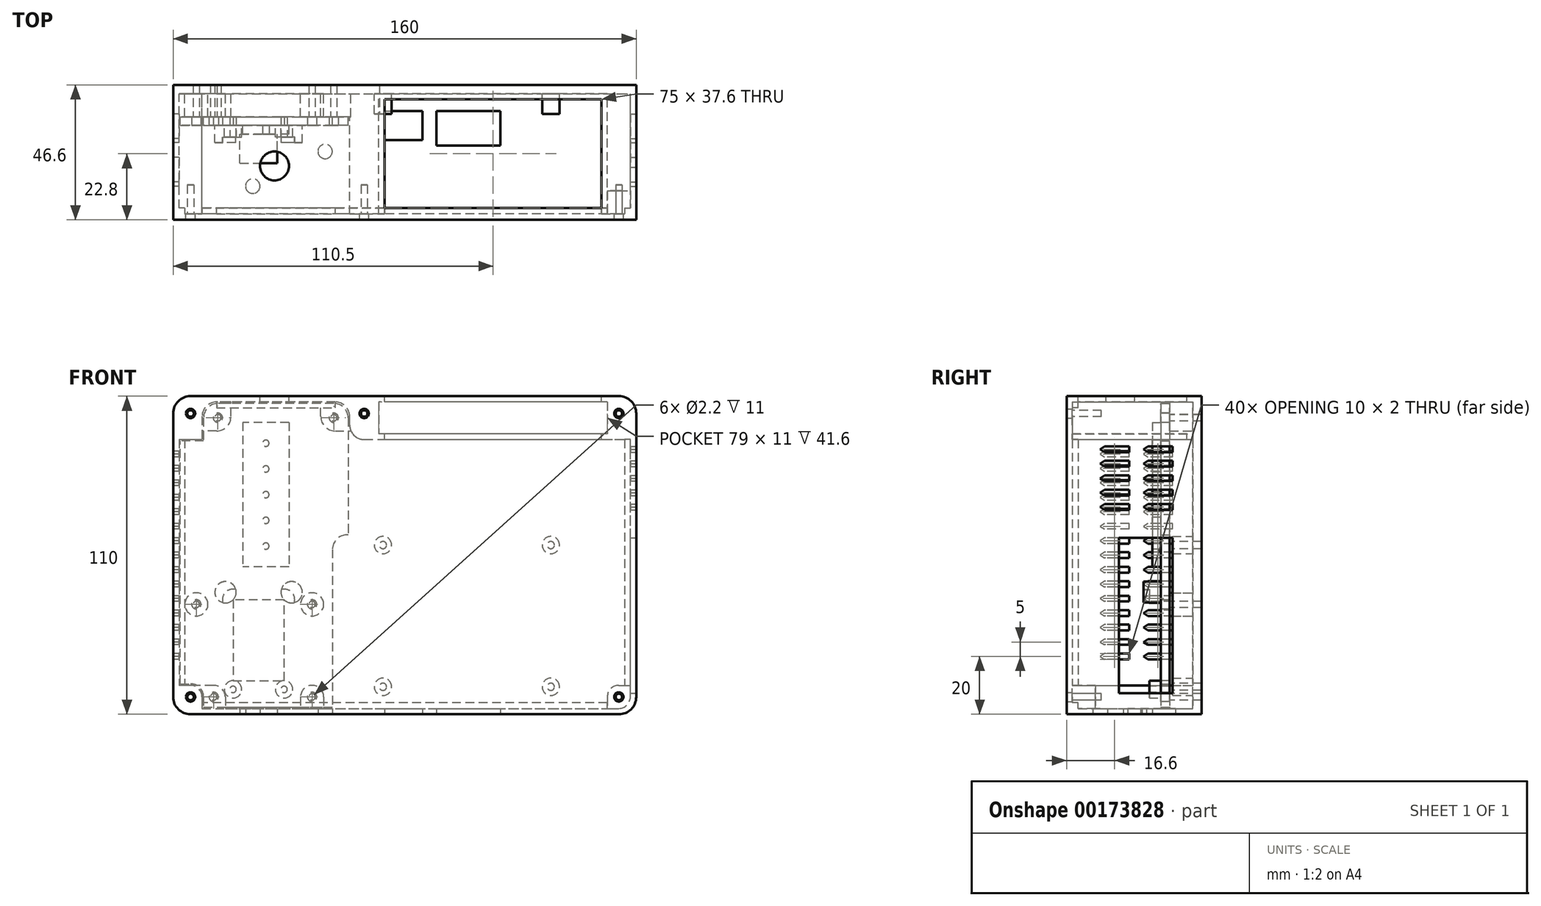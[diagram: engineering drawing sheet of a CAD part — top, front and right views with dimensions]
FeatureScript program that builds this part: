
annotation { "Feature Type Name" : "Feature", "Feature Type Description" : "" }
export const myFeature = defineFeature(function(context is Context, id is Id, definition is map)
    precondition{}
    {
        {
            var Q0;
            Q0=qCreatedBy(makeId("Front.planeOp"),FACE);
            var sketch = newSketch(context, id + "F0", { "sketchPlane" : qUnion([Q0])});
            skLineSegment(sketch, "E0.bottom", {"start": v(6, 0) * mm, "end": v(154, 0) * mm});
            skLineSegment(sketch, "E0.top", {"start": v(6, 110) * mm, "end": v(154, 110) * mm});
            skLineSegment(sketch, "E0.left", {"start": v(0, 6) * mm, "end": v(0, 104) * mm});
            skLineSegment(sketch, "E0.right", {"start": v(160, 6) * mm, "end": v(160, 104) * mm});
            skPoint(sketch, "E1.visualSharp", {"position": v(0, 110) * mm});
            skArc(sketch, "E1.filletArc", {"start": v(6, 110) * mm, "mid": v(1.76, 108.24) * mm, "end": v(0, 104) * mm});
            skPoint(sketch, "E2.visualSharp", {"position": v(160, 110) * mm});
            skArc(sketch, "E2.filletArc", {"start": v(160, 104) * mm, "mid": v(158.24, 108.24) * mm, "end": v(154, 110) * mm});
            skPoint(sketch, "E3.visualSharp", {"position": v(160, 0) * mm});
            skArc(sketch, "E3.filletArc", {"start": v(154, 0) * mm, "mid": v(158.24, 1.76) * mm, "end": v(160, 6) * mm});
            skPoint(sketch, "E4.visualSharp", {"position": v(0, 0) * mm});
            skArc(sketch, "E4.filletArc", {"start": v(0, 6) * mm, "mid": v(1.76, 1.76) * mm, "end": v(6, 0) * mm});
            skSolve(sketch);
        }
        {
            var Q0;
            Q0=makeQuery(id+"F0.imprint","IMPRINT",FACE,{"disambiguationData":[TD([[makeQuery(id+"F0.imprint","IMPRINT",EDGE,{"derivedFrom":sQuery(id+"F0.wireOp",EDGE,"E0.bottom")}),1.0]])]});
            extrude(context, id + "F1", {"entities" : qUnion([Q0]), "depth" : 3 * mm, "offsetDistance" : 25 * mm});
        }
        {
            var Q0;
            Q0=makeQuery(id+"F1.opExtrude","CAP_FACE",FACE,{"disambiguationData":[OSD([sQuery(id+"F0.wireOp",EDGE,"E0.bottom"),sQuery(id+"F0.wireOp",EDGE,"E0.top"),sQuery(id+"F0.wireOp",EDGE,"E0.left"),sQuery(id+"F0.wireOp",EDGE,"E0.right"),sQuery(id+"F0.wireOp",EDGE,"E1.filletArc"),sQuery(id+"F0.wireOp",EDGE,"E2.filletArc"),sQuery(id+"F0.wireOp",EDGE,"E3.filletArc"),sQuery(id+"F0.wireOp",EDGE,"E4.filletArc")])],"isStart":false});
            var sketch = newSketch(context, id + "F2", { "sketchPlane" : qUnion([Q0])});
            skLineSegment(sketch, "E5.bottom", {"start": v(150, 108) * mm, "end": v(150, 97) * mm});
            skLineSegment(sketch, "E5.top", {"start": v(71, 108) * mm, "end": v(71, 97) * mm});
            skLineSegment(sketch, "E5.left", {"start": v(150, 108) * mm, "end": v(80, 108) * mm});
            skLineSegment(sketch, "E5.right", {"start": v(150, 97) * mm, "end": v(71, 97) * mm});
            skLineSegment(sketch, "E6", {"start": v(71, 97) * mm, "end": v(71, 68) * mm, "construction": true});
            skLineSegment(sketch, "E7", {"start": v(71, 68) * mm, "end": v(150, 68) * mm, "construction": true});
            skLineSegment(sketch, "E8", {"start": v(150, 68) * mm, "end": v(150, 97) * mm, "construction": true});
            skLineSegment(sketch, "E9", {"start": v(71, 73) * mm, "end": v(150, 73) * mm, "construction": true});
            skLineSegment(sketch, "E10", {"start": v(80, 108) * mm, "end": v(71, 108) * mm});
            skPoint(sketch, "E11", {"position": v(80, 110) * mm});
            skLineSegment(sketch, "E12", {"start": v(2, 95) * mm, "end": v(10, 95) * mm});
            skLineSegment(sketch, "E13.0", {"start": v(6, 110) * mm, "end": v(154, 110) * mm});
            skPoint(sketch, "E14.0", {"position": v(1.76, 108.24) * mm});
            skLineSegment(sketch, "E15.0", {"start": v(0, 95) * mm, "end": v(0, 104) * mm});
            skArc(sketch, "E16.0", {"start": v(160, 104) * mm, "mid": v(158.24, 108.24) * mm, "end": v(154, 110) * mm});
            skLineSegment(sketch, "E17.0", {"start": v(160, 95) * mm, "end": v(160, 104) * mm});
            skPoint(sketch, "E18.orphan", {"position": v(0, 6) * mm});
            skPoint(sketch, "E19.orphan", {"position": v(160, 6) * mm});
            skPoint(sketch, "E20.orphan", {"position": v(10, 108) * mm});
            skLineSegment(sketch, "E21", {"start": v(61, 100) * mm, "end": v(61, 103) * mm});
            skLineSegment(sketch, "E22", {"start": v(56, 108) * mm, "end": v(15, 108) * mm});
            skLineSegment(sketch, "E23", {"start": v(10, 103) * mm, "end": v(10, 95) * mm});
            skArc(sketch, "E24.filletArc", {"start": v(15, 108) * mm, "mid": v(11.46, 106.54) * mm, "end": v(10, 103) * mm});
            skLineSegment(sketch, "E25.trimOffspring", {"start": v(66, 95) * mm, "end": v(158, 95) * mm});
            skPoint(sketch, "E26.0", {"position": v(1.76, 1.76) * mm});
            skLineSegment(sketch, "E27.0", {"start": v(6, 0) * mm, "end": v(84.03, 0) * mm});
            skPoint(sketch, "E28.orphan", {"position": v(154, 0) * mm});
            skArc(sketch, "E29.0", {"start": v(6, 110) * mm, "mid": v(1.76, 108.24) * mm, "end": v(0, 104) * mm});
            skLineSegment(sketch, "E30.0", {"start": v(160, 6) * mm, "end": v(160, 104) * mm});
            skLineSegment(sketch, "E31.0", {"start": v(0, 6) * mm, "end": v(0, 104) * mm});
            skArc(sketch, "E32.0", {"start": v(0, 6) * mm, "mid": v(1.76, 1.76) * mm, "end": v(6, 0) * mm});
            skLineSegment(sketch, "E33.0.2", {"start": v(154, 110) * mm, "end": v(6, 110) * mm});
            skLineSegment(sketch, "E33.0.4", {"start": v(0, 104) * mm, "end": v(0, 6) * mm});
            skLineSegment(sketch, "E33.0.6", {"start": v(6, 0) * mm, "end": v(154, 0) * mm});
            skArc(sketch, "E33.0.7", {"start": v(154, 0) * mm, "mid": v(158.24, 1.76) * mm, "end": v(160, 6) * mm});
            skLineSegment(sketch, "E34.0", {"start": v(158, 6) * mm, "end": v(158, 95) * mm});
            skLineSegment(sketch, "E34.1", {"start": v(2, 95) * mm, "end": v(2, 10) * mm});
            skLineSegment(sketch, "E34.3", {"start": v(10, 2) * mm, "end": v(154, 2) * mm});
            skArc(sketch, "E34.4", {"start": v(154, 2) * mm, "mid": v(156.83, 3.17) * mm, "end": v(158, 6) * mm});
            skPoint(sketch, "E35.visualSharp", {"position": v(61, 108) * mm});
            skArc(sketch, "E35.filletArc", {"start": v(61, 103) * mm, "mid": v(59.54, 106.54) * mm, "end": v(56, 108) * mm});
            skPoint(sketch, "E36.visualSharp", {"position": v(61, 95) * mm});
            skArc(sketch, "E36.filletArc", {"start": v(61, 100) * mm, "mid": v(62.46, 96.46) * mm, "end": v(66, 95) * mm});
            skArc(sketch, "E37", {"start": v(10, 6) * mm, "mid": v(8.83, 8.83) * mm, "end": v(6, 10) * mm});
            skLineSegment(sketch, "E38", {"start": v(10, 6) * mm, "end": v(10, 2) * mm});
            skLineSegment(sketch, "E39", {"start": v(6, 10) * mm, "end": v(2, 10) * mm});
            skSolve(sketch);
        }
        {
            var Q0;
            Q0=makeQuery(id+"F2.imprint","IMPRINT",FACE,{"disambiguationData":[TD([[makeQuery(id+"F2.imprint","IMPRINT",EDGE,{"derivedFrom":sQuery(id+"F2.wireOp",EDGE,"E5.bottom")}),1.0]])]});
            extrude(context, id + "F3", {"entities" : qUnion([Q0]), "operationType" : NewBodyOperationType.ADD, "depth" : 41.6 * mm, "offsetDistance" : 25 * mm});
        }
        {
            var Q0;
            Q0=qCreatedBy(makeId("Front.planeOp"),FACE);
            var sketch = newSketch(context, id + "F4", { "sketchPlane" : qUnion([Q0])});
            skLineSegment(sketch, "E40.bottom", {"start": v(69, 9.5) * mm, "end": v(69, 58.5) * mm, "construction": true});
            skLineSegment(sketch, "E40.top", {"start": v(154, 9.5) * mm, "end": v(154, 58.5) * mm, "construction": true});
            skLineSegment(sketch, "E40.left", {"start": v(72.5, 6) * mm, "end": v(150.5, 6) * mm, "construction": true});
            skLineSegment(sketch, "E40.right", {"start": v(72.5, 62) * mm, "end": v(150.5, 62) * mm, "construction": true});
            skPoint(sketch, "E41.visualSharp", {"position": v(69, 6) * mm});
            skArc(sketch, "E41.filletArc", {"start": v(69, 9.5) * mm, "mid": v(70.03, 7.03) * mm, "end": v(72.5, 6) * mm, "construction": true});
            skPoint(sketch, "E42.visualSharp", {"position": v(69, 62) * mm});
            skArc(sketch, "E42.filletArc", {"start": v(72.5, 62) * mm, "mid": v(70.03, 60.97) * mm, "end": v(69, 58.5) * mm, "construction": true});
            skPoint(sketch, "E43.visualSharp", {"position": v(154, 62) * mm});
            skArc(sketch, "E43.filletArc", {"start": v(154, 58.5) * mm, "mid": v(152.97, 60.97) * mm, "end": v(150.5, 62) * mm, "construction": true});
            skPoint(sketch, "E44.visualSharp", {"position": v(154, 6) * mm});
            skArc(sketch, "E44.filletArc", {"start": v(150.5, 6) * mm, "mid": v(152.97, 7.03) * mm, "end": v(154, 9.5) * mm, "construction": true});
            skCircle(sketch, "E45", {"center": v(72.5, 58.5) * mm, "radius": 3 * mm});
            skCircle(sketch, "E46", {"center": v(130.5, 58.5) * mm, "radius": 3 * mm});
            skCircle(sketch, "E47", {"center": v(130.5, 9.5) * mm, "radius": 3 * mm});
            skCircle(sketch, "E48", {"center": v(72.5, 9.5) * mm, "radius": 3 * mm});
            skPoint(sketch, "E49.0", {"position": v(6, 104) * mm});
            skPoint(sketch, "E50.0", {"position": v(154, 104) * mm});
            skPoint(sketch, "E51.0", {"position": v(6, 6) * mm});
            skPoint(sketch, "E52.orphan", {"position": v(6, 0) * mm});
            skPoint(sketch, "E53.0.end.orphan", {"position": v(160, 104) * mm});
            skPoint(sketch, "E53.0.start.orphan", {"position": v(160, 6) * mm});
            skSolve(sketch);
        }
        {
            var Q0;
            Q0=makeQuery(id+"F3.boolean.opBoolean","MERGE",FACE,{"derivedFrom":[makeQuery(id+"F1.opExtrude","SWEPT_FACE",FACE,{"disambiguationData":[OSD([sQuery(id+"F0.wireOp",EDGE,"E0.top")])]}),makeQuery(id+"F3.opExtrude","SWEPT_FACE",FACE,{"disambiguationData":[OSD([sQuery(id+"F2.wireOp",EDGE,"E13.0")])]})]});
            var sketch = newSketch(context, id + "F5", { "sketchPlane" : qUnion([Q0])});
            skLineSegment(sketch, "E54.bottom", {"start": v(73, -44.6) * mm, "end": v(148, -44.6) * mm});
            skLineSegment(sketch, "E54.top", {"start": v(73, -5) * mm, "end": v(148, -5) * mm});
            skLineSegment(sketch, "E54.left", {"start": v(73, -44.6) * mm, "end": v(73, -5) * mm});
            skLineSegment(sketch, "E54.right", {"start": v(148, -44.6) * mm, "end": v(148, -5) * mm});
            skLineSegment(sketch, "E55.0", {"start": v(71, -44.6) * mm, "end": v(71, -3) * mm});
            skLineSegment(sketch, "E56.0", {"start": v(150, -44.6) * mm, "end": v(150, -3) * mm});
            skLineSegment(sketch, "E57.0", {"start": v(150, -3) * mm, "end": v(71, -3) * mm});
            skSolve(sketch);
        }
        {
            var Q0;
            Q0 = qSketchRegion(id + "F5", true);
            extrude(context, id + "F6", {"entities" : qUnion([Q0]), "operationType" : NewBodyOperationType.REMOVE, "oppositeDirection" : true, "depth" : 19.9 * mm, "offsetDistance" : 25 * mm});
        }
        {
            var Q0;
            Q0 = qSketchRegion(id + "F4", true);
            var Q1;
            Q1=sQuery(id+"F4.wireOp",EDGE,"E46");
            var Q2;
            Q2=sQuery(id+"F4.wireOp",EDGE,"E45");
            var Q3;
            Q3=sQuery(id+"F4.wireOp",EDGE,"E48");
            var Q4;
            Q4=sQuery(id+"F4.wireOp",EDGE,"E47");
            extrude(context, id + "F7", {"entities" : qUnion([Q0]), "operationType" : NewBodyOperationType.ADD, "surfaceEntities" : qUnion([Q1, Q2, Q3, Q4]), "depth" : 10 * mm, "offsetDistance" : 25 * mm});
        }
        {
            var Q0;
            Q0=makeQuery(id+"F7.opExtrude","CAP_FACE",FACE,{"disambiguationData":[OSD([sQuery(id+"F4.wireOp",EDGE,"E45")])],"isStart":false});
            var sketch = newSketch(context, id + "F8", { "sketchPlane" : qUnion([Q0])});
            skPoint(sketch, "E58.0", {"position": v(72.5, 58.5) * mm});
            skPoint(sketch, "E59.0", {"position": v(130.5, 58.5) * mm});
            skPoint(sketch, "E60.0", {"position": v(130.5, 9.5) * mm});
            skPoint(sketch, "E61.0", {"position": v(72.5, 9.5) * mm});
            skCircle(sketch, "E62", {"center": v(72.5, 58.5) * mm, "radius": 1.25 * mm});
            skCircle(sketch, "E63", {"center": v(130.5, 58.5) * mm, "radius": 1.25 * mm});
            skCircle(sketch, "E64", {"center": v(130.5, 9.5) * mm, "radius": 1.25 * mm});
            skCircle(sketch, "E65", {"center": v(72.5, 9.5) * mm, "radius": 1.25 * mm});
            skSolve(sketch);
        }
        {
            var Q0;
            Q0 = qSketchRegion(id + "F8", true);
            extrude(context, id + "F9", {"entities" : qUnion([Q0]), "operationType" : NewBodyOperationType.REMOVE, "endBound" : BoundingType.UP_TO_NEXT, "oppositeDirection" : true, "depth" : 25 * mm, "offsetDistance" : 25 * mm});
        }
        {
            var Q0;
            Q0=qCreatedBy(makeId("Front.planeOp"),FACE);
            cPlane(context, id + "F10", {"entities" : qUnion([Q0]), "cplaneType" : CPlaneType.OFFSET, "offset" : 11 * mm, "width" : 150 * mm, "height" : 150 * mm});
        }
        {
            var Q0;
            Q0=qCreatedBy(id+"F10.planeOp",FACE);
            var sketch = newSketch(context, id + "F11", { "sketchPlane" : qUnion([Q0])});
            skPoint(sketch, "E66.0", {"position": v(10, 99) * mm});
            skPoint(sketch, "E67.0.start.orphan", {"position": v(61, 100) * mm});
            skLineSegment(sketch, "E68", {"start": v(60.5, 102.5) * mm, "end": v(60.5, 62) * mm});
            skPoint(sketch, "E69.0.start.orphan", {"position": v(15, 108) * mm});
            skPoint(sketch, "E70.0.start.orphan", {"position": v(10, 103) * mm});
            skPoint(sketch, "E71.end.orphan", {"position": v(10, 95) * mm});
            skPoint(sketch, "E72.0", {"position": v(35.5, 108) * mm});
            skPoint(sketch, "E73.0", {"position": v(6, 95) * mm});
            skLineSegment(sketch, "E74", {"start": v(55.5, 107.5) * mm, "end": v(15.45, 107.5) * mm});
            skLineSegment(sketch, "E75", {"start": v(10.5, 102.55) * mm, "end": v(10.5, 94.5) * mm});
            skLineSegment(sketch, "E76", {"start": v(10.5, 94.5) * mm, "end": v(2.5, 94.5) * mm});
            skPoint(sketch, "E77.visualSharp", {"position": v(10.5, 107.5) * mm});
            skArc(sketch, "E77.filletArc", {"start": v(15.45, 107.5) * mm, "mid": v(11.95, 106.05) * mm, "end": v(10.5, 102.55) * mm});
            skPoint(sketch, "E78.orphan", {"position": v(0, 104) * mm});
            skPoint(sketch, "E79.orphan", {"position": v(154, 0) * mm});
            skLineSegment(sketch, "E80.0", {"start": v(2.5, 10.5) * mm, "end": v(2.5, 94.5) * mm});
            skLineSegment(sketch, "E80.2", {"start": v(10.5, 2.5) * mm, "end": v(55, 2.5) * mm});
            skPoint(sketch, "E81.0.end.orphan", {"position": v(6, 0) * mm});
            skPoint(sketch, "E82.0.start.orphan", {"position": v(0, 6) * mm});
            skPoint(sketch, "E83.orphan", {"position": v(0, 94.5) * mm});
            skPoint(sketch, "E84.visualSharp", {"position": v(60.5, 107.5) * mm});
            skArc(sketch, "E84.filletArc", {"start": v(60.5, 102.5) * mm, "mid": v(59.04, 106.04) * mm, "end": v(55.5, 107.5) * mm});
            skPoint(sketch, "E85.0.start.orphan", {"position": v(56, 108) * mm});
            skLineSegment(sketch, "E86", {"start": v(55, 32.32) * mm, "end": v(55, 2.5) * mm});
            skPoint(sketch, "E87.0", {"position": v(69, 62) * mm});
            skLineSegment(sketch, "E88", {"start": v(60.5, 62) * mm, "end": v(60, 62) * mm});
            skLineSegment(sketch, "E89", {"start": v(55, 57) * mm, "end": v(55, 32.32) * mm});
            skPoint(sketch, "E90.visualSharp", {"position": v(55, 62) * mm});
            skArc(sketch, "E90.filletArc", {"start": v(60, 62) * mm, "mid": v(56.46, 60.54) * mm, "end": v(55, 57) * mm});
            skLineSegment(sketch, "E91", {"start": v(2.5, 10.5) * mm, "end": v(6, 10.5) * mm});
            skLineSegment(sketch, "E92", {"start": v(10.5, 6) * mm, "end": v(10.5, 2.5) * mm});
            skPoint(sketch, "E93.0", {"position": v(6, 6) * mm});
            skArc(sketch, "E94", {"start": v(10.5, 6) * mm, "mid": v(9.18, 9.18) * mm, "end": v(6, 10.5) * mm});
            skSolve(sketch);
        }
        {
            var Q0;
            Q0 = qSketchRegion(id + "F11", true);
            extrude(context, id + "F12", {"entities" : qUnion([Q0]), "depth" : 3 * mm, "offsetDistance" : 25 * mm});
        }
        {
            var Q0;
            Q0=makeQuery(id+"F3.boolean.opBoolean","MERGE",FACE,{"derivedFrom":[makeQuery(id+"F1.opExtrude","SWEPT_FACE",FACE,{"disambiguationData":[OSD([sQuery(id+"F0.wireOp",EDGE,"E0.right")])]}),makeQuery(id+"F3.opExtrude","SWEPT_FACE",FACE,{"disambiguationData":[OSD([sQuery(id+"F2.wireOp",EDGE,"E30.0")])]})]});
            var sketch = newSketch(context, id + "F13", { "sketchPlane" : qUnion([Q0])});
            skLineSegment(sketch, "E95.left", {"start": v(-28.5, 7.25) * mm, "end": v(-28.5, 44.5) * mm});
            skLineSegment(sketch, "E95.right", {"start": v(-10, 7.25) * mm, "end": v(-10, 16.25) * mm});
            skPoint(sketch, "E96.0", {"position": v(0, 6) * mm});
            skLineSegment(sketch, "E97", {"start": v(-10, 16.25) * mm, "end": v(-10, 45) * mm});
            skLineSegment(sketch, "E98.top", {"start": v(-10, 61) * mm, "end": v(-28.5, 61) * mm});
            skLineSegment(sketch, "E98.left", {"start": v(-10, 45) * mm, "end": v(-10, 53) * mm});
            skLineSegment(sketch, "E98.right", {"start": v(-28.5, 44.5) * mm, "end": v(-28.5, 61) * mm});
            skLineSegment(sketch, "E99", {"start": v(-10, 53) * mm, "end": v(-10, 61) * mm});
            skLineSegment(sketch, "E100", {"start": v(-10, 7.25) * mm, "end": v(-28.5, 7.25) * mm});
            skSolve(sketch);
        }
        {
            var Q0;
            Q0 = qSketchRegion(id + "F13", true);
            extrude(context, id + "F14", {"entities" : qUnion([Q0]), "operationType" : NewBodyOperationType.REMOVE, "endBound" : BoundingType.UP_TO_NEXT, "oppositeDirection" : true, "depth" : 25 * mm, "offsetDistance" : 25 * mm});
        }
        {
            var Q0;
            Q0=makeQuery(id+"F3.boolean.opBoolean","MERGE",FACE,{"derivedFrom":[makeQuery(id+"F1.opExtrude","SWEPT_FACE",FACE,{"disambiguationData":[OSD([sQuery(id+"F0.wireOp",EDGE,"E0.bottom")])]}),makeQuery(id+"F3.opExtrude","SWEPT_FACE",FACE,{"disambiguationData":[OSD([sQuery(id+"F2.wireOp",EDGE,"E33.0.6")])]})]});
            var sketch = newSketch(context, id + "F15", { "sketchPlane" : qUnion([Q0])});
            skLineSegment(sketch, "E101.bottom", {"start": v(73.1, 19) * mm, "end": v(73.1, 9) * mm});
            skLineSegment(sketch, "E101.top", {"start": v(86.1, 19) * mm, "end": v(86.1, 9) * mm});
            skLineSegment(sketch, "E101.left", {"start": v(73.1, 19) * mm, "end": v(86.1, 19) * mm});
            skLineSegment(sketch, "E101.right", {"start": v(73.1, 9) * mm, "end": v(79.6, 9) * mm});
            skPoint(sketch, "E102.0", {"position": v(72.93, 1.92) * mm});
            skLineSegment(sketch, "E103", {"start": v(79.6, 9) * mm, "end": v(86.1, 9) * mm});
            skLineSegment(sketch, "E104.bottom", {"start": v(91, 9) * mm, "end": v(91, 21) * mm});
            skLineSegment(sketch, "E104.top", {"start": v(113, 9) * mm, "end": v(113, 21) * mm});
            skLineSegment(sketch, "E104.left", {"start": v(91, 9) * mm, "end": v(102, 9) * mm});
            skLineSegment(sketch, "E104.right", {"start": v(91, 21) * mm, "end": v(113, 21) * mm});
            skLineSegment(sketch, "E105", {"start": v(102, 9) * mm, "end": v(113, 9) * mm});
            skLineSegment(sketch, "E106.bottom", {"start": v(23, 27) * mm, "end": v(23, 17) * mm});
            skLineSegment(sketch, "E106.top", {"start": v(36, 27) * mm, "end": v(36, 17) * mm});
            skLineSegment(sketch, "E106.left", {"start": v(23, 27) * mm, "end": v(36, 27) * mm});
            skLineSegment(sketch, "E106.right", {"start": v(23, 17) * mm, "end": v(29.5, 17) * mm});
            skLineSegment(sketch, "E107", {"start": v(29.5, 17) * mm, "end": v(36, 17) * mm});
            skSolve(sketch);
        }
        {
            var Q0;
            Q0=makeQuery(id+"F3.boolean.opBoolean","MERGE",FACE,{"derivedFrom":[makeQuery(id+"F1.opExtrude","SWEPT_FACE",FACE,{"disambiguationData":[OSD([sQuery(id+"F0.wireOp",EDGE,"E0.bottom")])]}),makeQuery(id+"F3.opExtrude","SWEPT_FACE",FACE,{"disambiguationData":[OSD([sQuery(id+"F2.wireOp",EDGE,"E33.0.6")])]})]});
            var sketch = newSketch(context, id + "F16", { "sketchPlane" : qUnion([Q0])});
            skCircle(sketch, "E108", {"center": v(27.5, 35) * mm, "radius": 2.5 * mm});
            skCircle(sketch, "E109", {"center": v(52.5, 23) * mm, "radius": 2.5 * mm});
            skPoint(sketch, "E110", {"position": v(34, 23) * mm});
            skPoint(sketch, "E111", {"position": v(27.5, 26) * mm});
            skSolve(sketch);
        }
        {
            var Q0;
            Q0=makeQuery(id+"F15.imprint","IMPRINT",FACE,{"disambiguationData":[TD([[makeQuery(id+"F15.imprint","IMPRINT",EDGE,{"derivedFrom":sQuery(id+"F15.wireOp",EDGE,"E106.bottom")}),1.0]])]});
            var Q1;
            Q1=makeQuery(id+"F15.imprint","IMPRINT",FACE,{"disambiguationData":[TD([[makeQuery(id+"F15.imprint","IMPRINT",EDGE,{"derivedFrom":sQuery(id+"F15.wireOp",EDGE,"E101.bottom")}),1.0]])]});
            var Q2;
            Q2=makeQuery(id+"F15.imprint","IMPRINT",FACE,{"disambiguationData":[TD([[makeQuery(id+"F15.imprint","IMPRINT",EDGE,{"derivedFrom":sQuery(id+"F15.wireOp",EDGE,"E104.bottom")}),-1.0]])]});
            var Q3;
            Q3 = qSketchRegion(id + "F16", true);
            extrude(context, id + "F17", {"entities" : qUnion([Q0, Q1, Q2, Q3]), "operationType" : NewBodyOperationType.REMOVE, "endBound" : BoundingType.UP_TO_NEXT, "oppositeDirection" : true, "depth" : 25 * mm, "offsetDistance" : 25 * mm});
        }
        {
            var Q0;
            Q0=makeQuery(id+"F12.opExtrude","CAP_FACE",FACE,{"disambiguationData":[OSD([sQuery(id+"F11.wireOp",EDGE,"E68"),sQuery(id+"F11.wireOp",EDGE,"E74"),sQuery(id+"F11.wireOp",EDGE,"E75"),sQuery(id+"F11.wireOp",EDGE,"E76"),sQuery(id+"F11.wireOp",EDGE,"E77.filletArc"),sQuery(id+"F11.wireOp",EDGE,"E80.0"),sQuery(id+"F11.wireOp",EDGE,"E80.1"),sQuery(id+"F11.wireOp",EDGE,"E80.2")])],"isStart":false});
            var sketch = newSketch(context, id + "F18", { "sketchPlane" : qUnion([Q0])});
            skLineSegment(sketch, "E112.bottom", {"start": v(20.68, 42.2) * mm, "end": v(38.32, 42.2) * mm, "construction": true});
            skLineSegment(sketch, "E112.top", {"start": v(20.67, 6) * mm, "end": v(29.5, 6) * mm, "construction": true});
            skLineSegment(sketch, "E112.left", {"start": v(18.07, 39.6) * mm, "end": v(18.07, 8.6) * mm, "construction": true});
            skLineSegment(sketch, "E112.right", {"start": v(40.93, 39.6) * mm, "end": v(40.93, 8.6) * mm, "construction": true});
            skPoint(sketch, "E113.visualSharp", {"position": v(18.07, 42.2) * mm});
            skArc(sketch, "E113.filletArc", {"start": v(20.67, 42.2) * mm, "mid": v(18.83, 41.44) * mm, "end": v(18.07, 39.6) * mm, "construction": true});
            skPoint(sketch, "E114.visualSharp", {"position": v(40.93, 42.2) * mm});
            skArc(sketch, "E114.filletArc", {"start": v(40.93, 39.6) * mm, "mid": v(40.17, 41.44) * mm, "end": v(38.32, 42.2) * mm});
            skPoint(sketch, "E115.visualSharp", {"position": v(40.93, 6) * mm});
            skArc(sketch, "E115.filletArc", {"start": v(38.33, 6) * mm, "mid": v(40.17, 6.76) * mm, "end": v(40.93, 8.6) * mm, "construction": true});
            skPoint(sketch, "E116.visualSharp", {"position": v(18.07, 6) * mm});
            skArc(sketch, "E116.filletArc", {"start": v(18.07, 8.6) * mm, "mid": v(18.83, 6.76) * mm, "end": v(20.67, 6) * mm, "construction": true});
            skCircle(sketch, "E117", {"center": v(20.68, 8.6) * mm, "radius": 1.1 * mm, "construction": true});
            skCircle(sketch, "E118", {"center": v(38.33, 8.6) * mm, "radius": 1.1 * mm, "construction": true});
            skCircle(sketch, "E119", {"center": v(20.68, 8.6) * mm, "radius": 3 * mm});
            skCircle(sketch, "E120", {"center": v(38.33, 8.6) * mm, "radius": 3 * mm});
            skCircle(sketch, "E121", {"center": v(40.93, 42.2) * mm, "radius": 3.68 * mm});
            skCircle(sketch, "E122", {"center": v(18.07, 42.2) * mm, "radius": 3.68 * mm});
            skLineSegment(sketch, "E123", {"start": v(29.5, 6) * mm, "end": v(38.33, 6) * mm, "construction": true});
            skSolve(sketch);
        }
        {
            var Q0;
            Q0 = qSketchRegion(id + "F18", true);
            extrude(context, id + "F19", {"entities" : qUnion([Q0]), "operationType" : NewBodyOperationType.ADD, "depth" : 4 * mm, "offsetDistance" : 25 * mm});
        }
        {
            var Q0;
            Q0=makeQuery(id+"F19.opExtrude","CAP_FACE",FACE,{"disambiguationData":[OSD([sQuery(id+"F18.wireOp",EDGE,"E119")])],"isStart":false});
            var sketch = newSketch(context, id + "F20", { "sketchPlane" : qUnion([Q0])});
            skPoint(sketch, "E124.0", {"position": v(20.68, 8.6) * mm});
            skPoint(sketch, "E125.0", {"position": v(38.33, 8.6) * mm});
            skCircle(sketch, "E126.0", {"center": v(20.68, 8.6) * mm, "radius": 1.1 * mm});
            skCircle(sketch, "E127.0", {"center": v(38.33, 8.6) * mm, "radius": 1.1 * mm});
            skSolve(sketch);
        }
        {
            var Q0;
            Q0 = qSketchRegion(id + "F20", true);
            extrude(context, id + "F21", {"entities" : qUnion([Q0]), "operationType" : NewBodyOperationType.REMOVE, "endBound" : BoundingType.UP_TO_NEXT, "oppositeDirection" : true, "depth" : 25 * mm, "offsetDistance" : 25 * mm});
        }
        {
            var Q0;
            Q0=makeQuery(id+"F18.imprint","IMPRINT",FACE,{"disambiguationData":[TD([[makeQuery(id+"F18.imprint","IMPRINT",EDGE,{"derivedFrom":sQuery(id+"F18.wireOp",EDGE,"E119")}),-1.0]])]});
            var sketch = newSketch(context, id + "F22", { "sketchPlane" : qUnion([Q0])});
            skLineSegment(sketch, "E128", {"start": v(20.68, 11.6) * mm, "end": v(20.68, 39.6) * mm});
            skLineSegment(sketch, "E129", {"start": v(20.68, 39.6) * mm, "end": v(38.32, 39.6) * mm});
            skLineSegment(sketch, "E130", {"start": v(38.32, 39.6) * mm, "end": v(38.32, 11.6) * mm});
            skLineSegment(sketch, "E131", {"start": v(38.32, 11.6) * mm, "end": v(20.68, 11.6) * mm});
            skPoint(sketch, "E132.0", {"position": v(20.68, 39.6) * mm});
            skPoint(sketch, "E133.0", {"position": v(38.32, 39.6) * mm});
            skSolve(sketch);
        }
        {
            var Q0;
            Q0 = qSketchRegion(id + "F22", true);
            extrude(context, id + "F23", {"entities" : qUnion([Q0]), "operationType" : NewBodyOperationType.REMOVE, "endBound" : BoundingType.UP_TO_NEXT, "oppositeDirection" : true, "depth" : 25 * mm, "offsetDistance" : 25 * mm});
        }
        {
            var Q0;
            Q0=makeQuery(id+"F19.opExtrude","CAP_FACE",FACE,{"disambiguationData":[OSD([sQuery(id+"F18.wireOp",EDGE,"E121")])],"isStart":false});
            var sketch = newSketch(context, id + "F24", { "sketchPlane" : qUnion([Q0])});
            skPoint(sketch, "E134.0", {"position": v(20.68, 39.6) * mm});
            skPoint(sketch, "E135.0", {"position": v(38.32, 39.6) * mm});
            skArc(sketch, "E136.0", {"start": v(21.63, 43.15) * mm, "mid": v(15.46, 44.8) * mm, "end": v(17.12, 38.64) * mm});
            skArc(sketch, "E137", {"start": v(21.63, 43.15) * mm, "mid": v(18.07, 42.2) * mm, "end": v(17.12, 38.64) * mm});
            skArc(sketch, "E138.converted", {"start": v(41.88, 38.64) * mm, "mid": v(43.53, 44.8) * mm, "end": v(37.37, 43.15) * mm});
            skArc(sketch, "E139.converted", {"start": v(41.88, 38.64) * mm, "mid": v(40.93, 42.2) * mm, "end": v(37.37, 43.15) * mm});
            skSolve(sketch);
        }
        {
            var Q0;
            Q0=makeQuery(id+"F24.imprint","IMPRINT",FACE,{"disambiguationData":[TD([[makeQuery(id+"F24.imprint","IMPRINT",EDGE,{"derivedFrom":sQuery(id+"F24.wireOp",EDGE,"E136.0")}),1.0]])]});
            var Q1;
            Q1=makeQuery(id+"F24.imprint","IMPRINT",FACE,{"disambiguationData":[TD([[makeQuery(id+"F24.imprint","IMPRINT",EDGE,{"derivedFrom":sQuery(id+"F24.wireOp",EDGE,"E138.converted")}),1.0]])]});
            extrude(context, id + "F25", {"entities" : qUnion([Q0, Q1]), "operationType" : NewBodyOperationType.ADD, "depth" : 2 * mm, "offsetDistance" : 25 * mm});
        }
        {
            var Q0;
            Q0=makeQuery(id+"F12.opExtrude","CAP_FACE",FACE,{"disambiguationData":[OSD([sQuery(id+"F11.wireOp",EDGE,"E68"),sQuery(id+"F11.wireOp",EDGE,"E74"),sQuery(id+"F11.wireOp",EDGE,"E75"),sQuery(id+"F11.wireOp",EDGE,"E76"),sQuery(id+"F11.wireOp",EDGE,"E77.filletArc"),sQuery(id+"F11.wireOp",EDGE,"E80.0"),sQuery(id+"F11.wireOp",EDGE,"E80.1"),sQuery(id+"F11.wireOp",EDGE,"E80.2")])],"isStart":false});
            var sketch = newSketch(context, id + "F26", { "sketchPlane" : qUnion([Q0])});
            skLineSegment(sketch, "E140.top", {"start": v(24.02, 100.94) * mm, "end": v(24.02, 50.94) * mm});
            skLineSegment(sketch, "E140.left", {"start": v(40.02, 100.94) * mm, "end": v(32.02, 100.94) * mm});
            skLineSegment(sketch, "E140.right", {"start": v(40.02, 50.94) * mm, "end": v(24.02, 50.94) * mm});
            skLineSegment(sketch, "E141", {"start": v(40.02, 100.94) * mm, "end": v(40.02, 75.94) * mm});
            skLineSegment(sketch, "E142", {"start": v(40.02, 75.94) * mm, "end": v(40.02, 50.94) * mm});
            skLineSegment(sketch, "E143", {"start": v(32.02, 100.94) * mm, "end": v(24.02, 100.94) * mm});
            skPoint(sketch, "E144", {"position": v(32.02, 58.16) * mm});
            skPoint(sketch, "E145.0.1.0", {"position": v(32.02, 67.05) * mm});
            skPoint(sketch, "E145.0.2.0", {"position": v(32.02, 75.94) * mm});
            skPoint(sketch, "E145.0.3.0", {"position": v(32.02, 84.83) * mm});
            skPoint(sketch, "E145.0.4.0", {"position": v(32.02, 93.72) * mm});
            skLineSegment(sketch, "E145.direction1", {"start": v(32.02, 58.16) * mm, "end": v(57.02, 58.16) * mm, "construction": true});
            skLineSegment(sketch, "E145.direction2", {"start": v(32.02, 58.16) * mm, "end": v(32.02, 67.05) * mm, "construction": true});
            skSolve(sketch);
        }
        {
            var Q0;
            Q0 = qSketchRegion(id + "F26", true);
            extrude(context, id + "F27", {"entities" : qUnion([Q0]), "operationType" : NewBodyOperationType.ADD, "depth" : 3 * mm, "offsetDistance" : 25 * mm});
        }
        {
            var Q0;
            Q0=sQuery(id+"F26.wireOp",VERTEX,"E145.0.4.0");
            var Q1;
            Q1=sQuery(id+"F26.wireOp",VERTEX,"E145.0.3.0");
            var Q2;
            Q2=sQuery(id+"F26.wireOp",VERTEX,"E145.0.2.0");
            var Q3;
            Q3=sQuery(id+"F26.wireOp",VERTEX,"E145.0.1.0");
            var Q4;
            Q4=sQuery(id+"F26.wireOp",VERTEX,"E144");
            var Q5;
            Q5=makeQuery(id+"F12.opExtrude","SWEPT_BODY",BODY,{"disambiguationData":[OSD([sQuery(id+"F11.wireOp",EDGE,"E68"),sQuery(id+"F11.wireOp",EDGE,"E74"),sQuery(id+"F11.wireOp",EDGE,"E75"),sQuery(id+"F11.wireOp",EDGE,"E76"),sQuery(id+"F11.wireOp",EDGE,"E77.filletArc"),sQuery(id+"F11.wireOp",EDGE,"E80.0"),sQuery(id+"F11.wireOp",EDGE,"E80.1"),sQuery(id+"F11.wireOp",EDGE,"E80.2"),sQuery(id+"F11.wireOp",EDGE,"E84.filletArc"),sQuery(id+"F11.wireOp",EDGE,"E86"),sQuery(id+"F11.wireOp",EDGE,"E88"),sQuery(id+"F11.wireOp",EDGE,"E89"),sQuery(id+"F11.wireOp",EDGE,"E90.filletArc")])]});
            hole(context, id + "F28", {"style" : HoleStyle.SIMPLE, "endStyle" : HoleEndStyle.THROUGH, "oppositeDirection" : true, "holeDiameter" : 2.2 * mm, "majorDiameter" : 5 * mm, "isTappedThrough" : true, "tappedDepth" : 12 * mm, "tapClearance" : 3, "locations" : qUnion([Q0, Q1, Q2, Q3, Q4]), "scope" : qUnion([Q5])});
        }
        {
            var Q0;
            Q0=makeQuery(id+"F3.boolean.opBoolean","SPLIT",FACE,{"disambiguationData":[TD([makeQuery(id+"F3.opExtrude","SWEPT_FACE",FACE,{"disambiguationData":[OSD([sQuery(id+"F2.wireOp",EDGE,"E12")])]})])],"derivedFrom":makeQuery(id+"F1.opExtrude","CAP_FACE",FACE,{"disambiguationData":[OSD([sQuery(id+"F0.wireOp",EDGE,"E0.bottom"),sQuery(id+"F0.wireOp",EDGE,"E0.top"),sQuery(id+"F0.wireOp",EDGE,"E0.left"),sQuery(id+"F0.wireOp",EDGE,"E0.right"),sQuery(id+"F0.wireOp",EDGE,"E1.filletArc"),sQuery(id+"F0.wireOp",EDGE,"E2.filletArc"),sQuery(id+"F0.wireOp",EDGE,"E3.filletArc"),sQuery(id+"F0.wireOp",EDGE,"E4.filletArc")])],"isStart":false})});
            var sketch = newSketch(context, id + "F29", { "sketchPlane" : qUnion([Q0])});
            skArc(sketch, "E146", {"start": v(15, 98) * mm, "mid": v(18.54, 99.46) * mm, "end": v(20, 103) * mm});
            skArc(sketch, "E147", {"start": v(51, 103) * mm, "mid": v(52.46, 99.46) * mm, "end": v(56, 98) * mm});
            skArc(sketch, "E148", {"start": v(44, 6) * mm, "mid": v(48, 10) * mm, "end": v(52, 6) * mm});
            skCircle(sketch, "E149", {"center": v(8, 38) * mm, "radius": 4 * mm});
            skCircle(sketch, "E150", {"center": v(48, 38) * mm, "radius": 4 * mm});
            skArc(sketch, "E151", {"start": v(18, 6) * mm, "mid": v(16.83, 8.83) * mm, "end": v(14, 10) * mm});
            skArc(sketch, "E152.0", {"start": v(10, 6) * mm, "mid": v(8.83, 8.83) * mm, "end": v(6, 10) * mm});
            skLineSegment(sketch, "E153.0", {"start": v(10, 6) * mm, "end": v(10, 2) * mm});
            skLineSegment(sketch, "E154.0.4", {"start": v(52, 2) * mm, "end": v(44, 2) * mm});
            skLineSegment(sketch, "E154.0.5", {"start": v(10, 2) * mm, "end": v(10, 6) * mm});
            skLineSegment(sketch, "E154.0.10", {"start": v(10, 98) * mm, "end": v(10, 103) * mm});
            skArc(sketch, "E154.0.11", {"start": v(10, 103) * mm, "mid": v(11.46, 106.54) * mm, "end": v(15, 108) * mm});
            skLineSegment(sketch, "E154.0.12", {"start": v(15, 108) * mm, "end": v(20, 108) * mm});
            skArc(sketch, "E154.0.13", {"start": v(56, 108) * mm, "mid": v(59.54, 106.54) * mm, "end": v(61, 103) * mm});
            skLineSegment(sketch, "E154.0.14", {"start": v(61, 103) * mm, "end": v(61, 100) * mm});
            skArc(sketch, "E154.0.15", {"start": v(61, 100) * mm, "mid": v(61.1, 98.98) * mm, "end": v(61.42, 98) * mm});
            skLineSegment(sketch, "E155", {"start": v(14, 10) * mm, "end": v(6, 10) * mm});
            skLineSegment(sketch, "E156", {"start": v(18, 6) * mm, "end": v(18, 2) * mm});
            skLineSegment(sketch, "E157", {"start": v(44, 6) * mm, "end": v(44, 2) * mm});
            skLineSegment(sketch, "E158", {"start": v(52, 6) * mm, "end": v(52, 2) * mm});
            skLineSegment(sketch, "E159.trimOffspring", {"start": v(18, 2) * mm, "end": v(10, 2) * mm});
            skLineSegment(sketch, "E160", {"start": v(20, 103) * mm, "end": v(20, 108) * mm});
            skLineSegment(sketch, "E161", {"start": v(15, 98) * mm, "end": v(10, 98) * mm});
            skLineSegment(sketch, "E162", {"start": v(51, 103) * mm, "end": v(51, 108) * mm});
            skLineSegment(sketch, "E163", {"start": v(56, 98) * mm, "end": v(61.42, 98) * mm});
            skLineSegment(sketch, "E164.trimOffspring", {"start": v(51, 108) * mm, "end": v(56, 108) * mm});
            skPoint(sketch, "E154.0.9.end.orphan", {"position": v(10, 95) * mm});
            skPoint(sketch, "E154.0.8.end.orphan", {"position": v(2, 95) * mm});
            skPoint(sketch, "E154.0.7.end.orphan", {"position": v(2, 10) * mm});
            skPoint(sketch, "E154.0.23.end.orphan", {"position": v(0, 104) * mm});
            skPoint(sketch, "E154.0.23.start.orphan", {"position": v(6, 110) * mm});
            skSolve(sketch);
        }
        {
            var Q0;
            Q0 = qSketchRegion(id + "F29", true);
            var Q1;
            Q1=makeQuery(id+"F12.opExtrude","SWEPT_BODY",BODY,{"disambiguationData":[OSD([sQuery(id+"F11.wireOp",EDGE,"E68"),sQuery(id+"F11.wireOp",EDGE,"E74"),sQuery(id+"F11.wireOp",EDGE,"E75"),sQuery(id+"F11.wireOp",EDGE,"E76"),sQuery(id+"F11.wireOp",EDGE,"E77.filletArc"),sQuery(id+"F11.wireOp",EDGE,"E80.0"),sQuery(id+"F11.wireOp",EDGE,"E80.1"),sQuery(id+"F11.wireOp",EDGE,"E80.2"),sQuery(id+"F11.wireOp",EDGE,"E84.filletArc"),sQuery(id+"F11.wireOp",EDGE,"E86"),sQuery(id+"F11.wireOp",EDGE,"E88"),sQuery(id+"F11.wireOp",EDGE,"E89"),sQuery(id+"F11.wireOp",EDGE,"E90.filletArc")])]});
            extrude(context, id + "F30", {"entities" : qUnion([Q0]), "operationType" : NewBodyOperationType.ADD, "depth" : 8 * mm, "endBoundEntityBody" : qUnion([Q1]), "offsetDistance" : 25 * mm});
        }
        {
            var Q0;
            Q0=makeQuery(id+"F18.imprint","IMPRINT",FACE,{"disambiguationData":[TD([[makeQuery(id+"F18.imprint","IMPRINT",EDGE,{"derivedFrom":sQuery(id+"F18.wireOp",EDGE,"E119")}),-1.0]])]});
            var sketch = newSketch(context, id + "F31", { "sketchPlane" : qUnion([Q0])});
            skPoint(sketch, "E165.0", {"position": v(15.45, 102.55) * mm});
            skPoint(sketch, "E166.0", {"position": v(55.5, 102.5) * mm});
            skPoint(sketch, "E167.0", {"position": v(48, 38) * mm});
            skPoint(sketch, "E168.0", {"position": v(8, 38) * mm});
            skPoint(sketch, "E169.0", {"position": v(14, 6) * mm});
            skPoint(sketch, "E170.0", {"position": v(48, 6) * mm});
            skCircle(sketch, "E171", {"center": v(15.45, 102.55) * mm, "radius": 1.6 * mm});
            skCircle(sketch, "E172", {"center": v(55.5, 102.5) * mm, "radius": 1.6 * mm});
            skCircle(sketch, "E173", {"center": v(48, 38) * mm, "radius": 1.6 * mm});
            skCircle(sketch, "E174", {"center": v(48, 6) * mm, "radius": 1.6 * mm});
            skCircle(sketch, "E175", {"center": v(14, 6) * mm, "radius": 1.6 * mm});
            skCircle(sketch, "E176", {"center": v(8, 38) * mm, "radius": 1.6 * mm});
            skPoint(sketch, "E177.0.11.end.orphan", {"position": v(2.5, 94.5) * mm});
            skPoint(sketch, "E177.0.10.end.orphan", {"position": v(10.5, 94.5) * mm});
            skPoint(sketch, "E177.0.9.end.orphan", {"position": v(10.5, 102.55) * mm});
            skPoint(sketch, "E177.0.8.end.orphan", {"position": v(15.45, 107.5) * mm});
            skPoint(sketch, "E177.0.7.end.orphan", {"position": v(55.5, 107.5) * mm});
            skPoint(sketch, "E177.0.6.end.orphan", {"position": v(60.5, 102.5) * mm});
            skPoint(sketch, "E177.0.3.end.orphan", {"position": v(55, 57) * mm});
            skPoint(sketch, "E177.0.2.end.orphan", {"position": v(55, 2.5) * mm});
            skPoint(sketch, "E177.0.1.end.orphan", {"position": v(10.5, 2.5) * mm});
            skPoint(sketch, "E177.0.0.end.orphan", {"position": v(10.5, 6) * mm});
            skPoint(sketch, "E177.0.13.end.orphan", {"position": v(6, 10.5) * mm});
            skPoint(sketch, "E177.0.13.start.orphan", {"position": v(2.5, 10.5) * mm});
            skPoint(sketch, "E177.0.5.end.orphan", {"position": v(60.5, 62) * mm});
            skPoint(sketch, "E177.0.5.start.orphan", {"position": v(60, 62) * mm});
            skSolve(sketch);
        }
        {
            var Q0;
            Q0 = qSketchRegion(id + "F31", true);
            extrude(context, id + "F32", {"entities" : qUnion([Q0]), "operationType" : NewBodyOperationType.REMOVE, "oppositeDirection" : true, "depth" : 3 * mm, "offsetDistance" : 25 * mm});
        }
        {
            var Q0;
            Q0=qCreatedBy(id+"F10.planeOp",FACE);
            var sketch = newSketch(context, id + "F33", { "sketchPlane" : qUnion([Q0])});
            skPoint(sketch, "E178.0", {"position": v(15.45, 102.55) * mm});
            skPoint(sketch, "E179.0", {"position": v(55.5, 102.5) * mm});
            skPoint(sketch, "E180.0", {"position": v(48, 38) * mm});
            skPoint(sketch, "E181.0", {"position": v(14, 6) * mm});
            skPoint(sketch, "E182.0", {"position": v(8, 38) * mm});
            skCircle(sketch, "E183", {"center": v(15.45, 102.55) * mm, "radius": 1.1 * mm});
            skCircle(sketch, "E184", {"center": v(55.5, 102.5) * mm, "radius": 1.1 * mm});
            skCircle(sketch, "E185", {"center": v(48, 38) * mm, "radius": 1.1 * mm});
            skCircle(sketch, "E186", {"center": v(48, 6) * mm, "radius": 1.1 * mm});
            skCircle(sketch, "E187", {"center": v(14, 6) * mm, "radius": 1.1 * mm});
            skCircle(sketch, "E188", {"center": v(8, 38) * mm, "radius": 1.1 * mm});
            skPoint(sketch, "E189.0", {"position": v(15, 103) * mm});
            skSolve(sketch);
        }
        {
            var Q0;
            Q0 = qSketchRegion(id + "F33", true);
            extrude(context, id + "F34", {"entities" : qUnion([Q0]), "operationType" : NewBodyOperationType.REMOVE, "endBound" : BoundingType.UP_TO_NEXT, "oppositeDirection" : true, "depth" : 25 * mm, "offsetDistance" : 25 * mm});
        }
        {
            var Q0;
            Q0=makeQuery(id+"F3.boolean.opBoolean","MERGE",FACE,{"derivedFrom":[makeQuery(id+"F1.opExtrude","SWEPT_FACE",FACE,{"disambiguationData":[OSD([sQuery(id+"F0.wireOp",EDGE,"E0.top")])]}),makeQuery(id+"F3.opExtrude","SWEPT_FACE",FACE,{"disambiguationData":[OSD([sQuery(id+"F2.wireOp",EDGE,"E33.0.2")])]})]});
            var sketch = newSketch(context, id + "F35", { "sketchPlane" : qUnion([Q0])});
            skCircle(sketch, "E190", {"center": v(35, -28) * mm, "radius": 5 * mm});
            skSolve(sketch);
        }
        {
            var Q0;
            Q0 = qSketchRegion(id + "F35", true);
            extrude(context, id + "F36", {"entities" : qUnion([Q0]), "operationType" : NewBodyOperationType.REMOVE, "endBound" : BoundingType.UP_TO_NEXT, "oppositeDirection" : true, "depth" : 25 * mm, "offsetDistance" : 25 * mm});
        }
        {
            var Q0;
            Q0=makeQuery(id+"F3.opExtrude","CAP_FACE",FACE,{"disambiguationData":[OSD([sQuery(id+"F2.wireOp",EDGE,"E5.bottom"),sQuery(id+"F2.wireOp",EDGE,"E5.top"),sQuery(id+"F2.wireOp",EDGE,"E5.left"),sQuery(id+"F2.wireOp",EDGE,"E5.right"),sQuery(id+"F2.wireOp",EDGE,"E10"),sQuery(id+"F2.wireOp",EDGE,"E12"),sQuery(id+"F2.wireOp",EDGE,"E21"),sQuery(id+"F2.wireOp",EDGE,"E22"),sQuery(id+"F2.wireOp",EDGE,"E23"),sQuery(id+"F2.wireOp",EDGE,"E24.filletArc"),sQuery(id+"F2.wireOp",EDGE,"E25.trimOffspring"),sQuery(id+"F2.wireOp",EDGE,"E30.0"),sQuery(id+"F2.wireOp",EDGE,"E16.0"),sQuery(id+"F2.wireOp",EDGE,"E33.0.2"),sQuery(id+"F2.wireOp",EDGE,"E29.0"),sQuery(id+"F2.wireOp",EDGE,"E33.0.4"),sQuery(id+"F2.wireOp",EDGE,"E32.0"),sQuery(id+"F2.wireOp",EDGE,"E33.0.6"),sQuery(id+"F2.wireOp",EDGE,"E33.0.7"),sQuery(id+"F2.wireOp",EDGE,"E34.0"),sQuery(id+"F2.wireOp",EDGE,"E34.1"),sQuery(id+"F2.wireOp",EDGE,"E34.2"),sQuery(id+"F2.wireOp",EDGE,"E34.3"),sQuery(id+"F2.wireOp",EDGE,"E34.4"),sQuery(id+"F2.wireOp",EDGE,"E35.filletArc"),sQuery(id+"F2.wireOp",EDGE,"E36.filletArc")])],"isStart":false});
            var sketch = newSketch(context, id + "F37", { "sketchPlane" : qUnion([Q0])});
            skArc(sketch, "E191.0", {"start": v(154, 2) * mm, "mid": v(156.83, 3.17) * mm, "end": v(158, 6) * mm});
            skLineSegment(sketch, "E192.0", {"start": v(158, 6) * mm, "end": v(158, 10) * mm});
            skPoint(sketch, "E193.0", {"position": v(10, 4) * mm});
            skArc(sketch, "E194", {"start": v(154, 10) * mm, "mid": v(151.17, 8.83) * mm, "end": v(150, 6) * mm});
            skLineSegment(sketch, "E195", {"start": v(154, 10) * mm, "end": v(158, 10) * mm});
            skLineSegment(sketch, "E196", {"start": v(150, 6) * mm, "end": v(150, 2) * mm});
            skPoint(sketch, "E197.orphan", {"position": v(158, 95) * mm});
            skLineSegment(sketch, "E198.trimOffspring", {"start": v(150, 2) * mm, "end": v(154, 2) * mm});
            skPoint(sketch, "E199.orphan", {"position": v(2, 95) * mm});
            skPoint(sketch, "E200.0.start.orphan", {"position": v(10, 2) * mm});
            skPoint(sketch, "E201.0.end.orphan", {"position": v(2, 10) * mm});
            skPoint(sketch, "E201.0.start.orphan", {"position": v(6, 10) * mm});
            skPoint(sketch, "E202.0.start.orphan", {"position": v(10, 6) * mm});
            skSolve(sketch);
        }
        {
            var Q0;
            Q0 = qSketchRegion(id + "F37", true);
            extrude(context, id + "F38", {"entities" : qUnion([Q0]), "operationType" : NewBodyOperationType.ADD, "oppositeDirection" : true, "depth" : 8 * mm, "offsetDistance" : 25 * mm});
        }
        {
            var Q0;
            Q0=makeQuery(id+"F3.boolean.opBoolean","MERGE",FACE,{"derivedFrom":[makeQuery(id+"F1.opExtrude","SWEPT_FACE",FACE,{"disambiguationData":[OSD([sQuery(id+"F0.wireOp",EDGE,"E0.left")])]}),makeQuery(id+"F3.opExtrude","SWEPT_FACE",FACE,{"disambiguationData":[OSD([sQuery(id+"F2.wireOp",EDGE,"E33.0.4")])]})]});
            var sketch = newSketch(context, id + "F39", { "sketchPlane" : qUnion([Q0])});
            skLineSegment(sketch, "E203.bottom", {"start": v(10, 19) * mm, "end": v(18.5, 19) * mm});
            skLineSegment(sketch, "E203.top", {"start": v(10, 21) * mm, "end": v(18.5, 21) * mm});
            skLineSegment(sketch, "E203.left", {"start": v(10, 19) * mm, "end": v(10, 21) * mm});
            skLineSegment(sketch, "E204", {"start": v(18.5, 21) * mm, "end": v(20, 20) * mm});
            skLineSegment(sketch, "E205", {"start": v(20, 20) * mm, "end": v(18.5, 19) * mm});
            skLineSegment(sketch, "E206.0.1.0", {"start": v(20, 25) * mm, "end": v(18.5, 24) * mm});
            skLineSegment(sketch, "E206.0.1.1", {"start": v(10, 24) * mm, "end": v(18.5, 24) * mm});
            skLineSegment(sketch, "E206.0.1.2", {"start": v(18.5, 26) * mm, "end": v(20, 25) * mm});
            skLineSegment(sketch, "E206.0.1.3", {"start": v(10, 24) * mm, "end": v(10, 26) * mm});
            skLineSegment(sketch, "E206.0.1.4", {"start": v(10, 26) * mm, "end": v(18.5, 26) * mm});
            skLineSegment(sketch, "E206.0.2.0", {"start": v(20, 30) * mm, "end": v(18.5, 29) * mm});
            skLineSegment(sketch, "E206.0.2.1", {"start": v(10, 29) * mm, "end": v(18.5, 29) * mm});
            skLineSegment(sketch, "E206.0.2.2", {"start": v(18.5, 31) * mm, "end": v(20, 30) * mm});
            skLineSegment(sketch, "E206.0.2.3", {"start": v(10, 29) * mm, "end": v(10, 31) * mm});
            skLineSegment(sketch, "E206.0.2.4", {"start": v(10, 31) * mm, "end": v(18.5, 31) * mm});
            skLineSegment(sketch, "E206.0.3.0", {"start": v(20, 35) * mm, "end": v(18.5, 34) * mm});
            skLineSegment(sketch, "E206.0.3.1", {"start": v(10, 34) * mm, "end": v(18.5, 34) * mm});
            skLineSegment(sketch, "E206.0.3.2", {"start": v(18.5, 36) * mm, "end": v(20, 35) * mm});
            skLineSegment(sketch, "E206.0.3.3", {"start": v(10, 34) * mm, "end": v(10, 36) * mm});
            skLineSegment(sketch, "E206.0.3.4", {"start": v(10, 36) * mm, "end": v(18.5, 36) * mm});
            skLineSegment(sketch, "E206.0.4.0", {"start": v(20, 40) * mm, "end": v(18.5, 39) * mm});
            skLineSegment(sketch, "E206.0.4.1", {"start": v(10, 39) * mm, "end": v(18.5, 39) * mm});
            skLineSegment(sketch, "E206.0.4.2", {"start": v(18.5, 41) * mm, "end": v(20, 40) * mm});
            skLineSegment(sketch, "E206.0.4.3", {"start": v(10, 39) * mm, "end": v(10, 41) * mm});
            skLineSegment(sketch, "E206.0.4.4", {"start": v(10, 41) * mm, "end": v(18.5, 41) * mm});
            skLineSegment(sketch, "E206.0.5.0", {"start": v(20, 45) * mm, "end": v(18.5, 44) * mm});
            skLineSegment(sketch, "E206.0.5.1", {"start": v(10, 44) * mm, "end": v(18.5, 44) * mm});
            skLineSegment(sketch, "E206.0.5.2", {"start": v(18.5, 46) * mm, "end": v(20, 45) * mm});
            skLineSegment(sketch, "E206.0.5.3", {"start": v(10, 44) * mm, "end": v(10, 46) * mm});
            skLineSegment(sketch, "E206.0.5.4", {"start": v(10, 46) * mm, "end": v(18.5, 46) * mm});
            skLineSegment(sketch, "E206.0.6.0", {"start": v(20, 50) * mm, "end": v(18.5, 49) * mm});
            skLineSegment(sketch, "E206.0.6.1", {"start": v(10, 49) * mm, "end": v(18.5, 49) * mm});
            skLineSegment(sketch, "E206.0.6.2", {"start": v(18.5, 51) * mm, "end": v(20, 50) * mm});
            skLineSegment(sketch, "E206.0.6.3", {"start": v(10, 49) * mm, "end": v(10, 51) * mm});
            skLineSegment(sketch, "E206.0.6.4", {"start": v(10, 51) * mm, "end": v(18.5, 51) * mm});
            skLineSegment(sketch, "E206.0.7.0", {"start": v(20, 55) * mm, "end": v(18.5, 54) * mm});
            skLineSegment(sketch, "E206.0.7.1", {"start": v(10, 54) * mm, "end": v(18.5, 54) * mm});
            skLineSegment(sketch, "E206.0.7.2", {"start": v(18.5, 56) * mm, "end": v(20, 55) * mm});
            skLineSegment(sketch, "E206.0.7.3", {"start": v(10, 54) * mm, "end": v(10, 56) * mm});
            skLineSegment(sketch, "E206.0.7.4", {"start": v(10, 56) * mm, "end": v(18.5, 56) * mm});
            skLineSegment(sketch, "E206.0.8.0", {"start": v(20, 60) * mm, "end": v(18.5, 59) * mm});
            skLineSegment(sketch, "E206.0.8.1", {"start": v(10, 59) * mm, "end": v(18.5, 59) * mm});
            skLineSegment(sketch, "E206.0.8.2", {"start": v(18.5, 61) * mm, "end": v(20, 60) * mm});
            skLineSegment(sketch, "E206.0.8.3", {"start": v(10, 59) * mm, "end": v(10, 61) * mm});
            skLineSegment(sketch, "E206.0.8.4", {"start": v(10, 61) * mm, "end": v(18.5, 61) * mm});
            skLineSegment(sketch, "E206.0.9.0", {"start": v(20, 65) * mm, "end": v(18.5, 64) * mm});
            skLineSegment(sketch, "E206.0.9.1", {"start": v(10, 64) * mm, "end": v(18.5, 64) * mm});
            skLineSegment(sketch, "E206.0.9.2", {"start": v(18.5, 66) * mm, "end": v(20, 65) * mm});
            skLineSegment(sketch, "E206.0.9.3", {"start": v(10, 64) * mm, "end": v(10, 66) * mm});
            skLineSegment(sketch, "E206.0.9.4", {"start": v(10, 66) * mm, "end": v(18.5, 66) * mm});
            skLineSegment(sketch, "E206.0.10.0", {"start": v(20, 70) * mm, "end": v(18.5, 69) * mm});
            skLineSegment(sketch, "E206.0.10.1", {"start": v(10, 69) * mm, "end": v(18.5, 69) * mm});
            skLineSegment(sketch, "E206.0.10.2", {"start": v(18.5, 71) * mm, "end": v(20, 70) * mm});
            skLineSegment(sketch, "E206.0.10.3", {"start": v(10, 69) * mm, "end": v(10, 71) * mm});
            skLineSegment(sketch, "E206.0.10.4", {"start": v(10, 71) * mm, "end": v(18.5, 71) * mm});
            skLineSegment(sketch, "E206.0.11.0", {"start": v(20, 75) * mm, "end": v(18.5, 74) * mm});
            skLineSegment(sketch, "E206.0.11.1", {"start": v(10, 74) * mm, "end": v(18.5, 74) * mm});
            skLineSegment(sketch, "E206.0.11.2", {"start": v(18.5, 76) * mm, "end": v(20, 75) * mm});
            skLineSegment(sketch, "E206.0.11.3", {"start": v(10, 74) * mm, "end": v(10, 76) * mm});
            skLineSegment(sketch, "E206.0.11.4", {"start": v(10, 76) * mm, "end": v(18.5, 76) * mm});
            skLineSegment(sketch, "E206.0.12.0", {"start": v(20, 80) * mm, "end": v(18.5, 79) * mm});
            skLineSegment(sketch, "E206.0.12.1", {"start": v(10, 79) * mm, "end": v(18.5, 79) * mm});
            skLineSegment(sketch, "E206.0.12.2", {"start": v(18.5, 81) * mm, "end": v(20, 80) * mm});
            skLineSegment(sketch, "E206.0.12.3", {"start": v(10, 79) * mm, "end": v(10, 81) * mm});
            skLineSegment(sketch, "E206.0.12.4", {"start": v(10, 81) * mm, "end": v(18.5, 81) * mm});
            skLineSegment(sketch, "E206.0.13.0", {"start": v(20, 85) * mm, "end": v(18.5, 84) * mm});
            skLineSegment(sketch, "E206.0.13.1", {"start": v(10, 84) * mm, "end": v(18.5, 84) * mm});
            skLineSegment(sketch, "E206.0.13.2", {"start": v(18.5, 86) * mm, "end": v(20, 85) * mm});
            skLineSegment(sketch, "E206.0.13.3", {"start": v(10, 84) * mm, "end": v(10, 86) * mm});
            skLineSegment(sketch, "E206.0.13.4", {"start": v(10, 86) * mm, "end": v(18.5, 86) * mm});
            skLineSegment(sketch, "E206.0.14.0", {"start": v(20, 90) * mm, "end": v(18.5, 89) * mm});
            skLineSegment(sketch, "E206.0.14.1", {"start": v(10, 89) * mm, "end": v(18.5, 89) * mm});
            skLineSegment(sketch, "E206.0.14.2", {"start": v(18.5, 91) * mm, "end": v(20, 90) * mm});
            skLineSegment(sketch, "E206.0.14.3", {"start": v(10, 89) * mm, "end": v(10, 91) * mm});
            skLineSegment(sketch, "E206.0.14.4", {"start": v(10, 91) * mm, "end": v(18.5, 91) * mm});
            skLineSegment(sketch, "E206.1.0.0", {"start": v(35, 20) * mm, "end": v(33.5, 19) * mm});
            skLineSegment(sketch, "E206.1.0.1", {"start": v(25, 19) * mm, "end": v(33.5, 19) * mm});
            skLineSegment(sketch, "E206.1.0.2", {"start": v(33.5, 21) * mm, "end": v(35, 20) * mm});
            skLineSegment(sketch, "E206.1.0.3", {"start": v(25, 19) * mm, "end": v(25, 21) * mm});
            skLineSegment(sketch, "E206.1.0.4", {"start": v(25, 21) * mm, "end": v(33.5, 21) * mm});
            skLineSegment(sketch, "E206.1.1.0", {"start": v(35, 25) * mm, "end": v(33.5, 24) * mm});
            skLineSegment(sketch, "E206.1.1.1", {"start": v(25, 24) * mm, "end": v(33.5, 24) * mm});
            skLineSegment(sketch, "E206.1.1.2", {"start": v(33.5, 26) * mm, "end": v(35, 25) * mm});
            skLineSegment(sketch, "E206.1.1.3", {"start": v(25, 24) * mm, "end": v(25, 26) * mm});
            skLineSegment(sketch, "E206.1.1.4", {"start": v(25, 26) * mm, "end": v(33.5, 26) * mm});
            skLineSegment(sketch, "E206.1.2.0", {"start": v(35, 30) * mm, "end": v(33.5, 29) * mm});
            skLineSegment(sketch, "E206.1.2.1", {"start": v(25, 29) * mm, "end": v(33.5, 29) * mm});
            skLineSegment(sketch, "E206.1.2.2", {"start": v(33.5, 31) * mm, "end": v(35, 30) * mm});
            skLineSegment(sketch, "E206.1.2.3", {"start": v(25, 29) * mm, "end": v(25, 31) * mm});
            skLineSegment(sketch, "E206.1.2.4", {"start": v(25, 31) * mm, "end": v(33.5, 31) * mm});
            skLineSegment(sketch, "E206.1.3.0", {"start": v(35, 35) * mm, "end": v(33.5, 34) * mm});
            skLineSegment(sketch, "E206.1.3.1", {"start": v(25, 34) * mm, "end": v(33.5, 34) * mm});
            skLineSegment(sketch, "E206.1.3.2", {"start": v(33.5, 36) * mm, "end": v(35, 35) * mm});
            skLineSegment(sketch, "E206.1.3.3", {"start": v(25, 34) * mm, "end": v(25, 36) * mm});
            skLineSegment(sketch, "E206.1.3.4", {"start": v(25, 36) * mm, "end": v(33.5, 36) * mm});
            skLineSegment(sketch, "E206.1.4.0", {"start": v(35, 40) * mm, "end": v(33.5, 39) * mm});
            skLineSegment(sketch, "E206.1.4.1", {"start": v(25, 39) * mm, "end": v(33.5, 39) * mm});
            skLineSegment(sketch, "E206.1.4.2", {"start": v(33.5, 41) * mm, "end": v(35, 40) * mm});
            skLineSegment(sketch, "E206.1.4.3", {"start": v(25, 39) * mm, "end": v(25, 41) * mm});
            skLineSegment(sketch, "E206.1.4.4", {"start": v(25, 41) * mm, "end": v(33.5, 41) * mm});
            skLineSegment(sketch, "E206.1.5.0", {"start": v(35, 45) * mm, "end": v(33.5, 44) * mm});
            skLineSegment(sketch, "E206.1.5.1", {"start": v(25, 44) * mm, "end": v(33.5, 44) * mm});
            skLineSegment(sketch, "E206.1.5.2", {"start": v(33.5, 46) * mm, "end": v(35, 45) * mm});
            skLineSegment(sketch, "E206.1.5.3", {"start": v(25, 44) * mm, "end": v(25, 46) * mm});
            skLineSegment(sketch, "E206.1.5.4", {"start": v(25, 46) * mm, "end": v(33.5, 46) * mm});
            skLineSegment(sketch, "E206.1.6.0", {"start": v(35, 50) * mm, "end": v(33.5, 49) * mm});
            skLineSegment(sketch, "E206.1.6.1", {"start": v(25, 49) * mm, "end": v(33.5, 49) * mm});
            skLineSegment(sketch, "E206.1.6.2", {"start": v(33.5, 51) * mm, "end": v(35, 50) * mm});
            skLineSegment(sketch, "E206.1.6.3", {"start": v(25, 49) * mm, "end": v(25, 51) * mm});
            skLineSegment(sketch, "E206.1.6.4", {"start": v(25, 51) * mm, "end": v(33.5, 51) * mm});
            skLineSegment(sketch, "E206.1.7.0", {"start": v(35, 55) * mm, "end": v(33.5, 54) * mm});
            skLineSegment(sketch, "E206.1.7.1", {"start": v(25, 54) * mm, "end": v(33.5, 54) * mm});
            skLineSegment(sketch, "E206.1.7.2", {"start": v(33.5, 56) * mm, "end": v(35, 55) * mm});
            skLineSegment(sketch, "E206.1.7.3", {"start": v(25, 54) * mm, "end": v(25, 56) * mm});
            skLineSegment(sketch, "E206.1.7.4", {"start": v(25, 56) * mm, "end": v(33.5, 56) * mm});
            skLineSegment(sketch, "E206.1.8.0", {"start": v(35, 60) * mm, "end": v(33.5, 59) * mm});
            skLineSegment(sketch, "E206.1.8.1", {"start": v(25, 59) * mm, "end": v(33.5, 59) * mm});
            skLineSegment(sketch, "E206.1.8.2", {"start": v(33.5, 61) * mm, "end": v(35, 60) * mm});
            skLineSegment(sketch, "E206.1.8.3", {"start": v(25, 59) * mm, "end": v(25, 61) * mm});
            skLineSegment(sketch, "E206.1.8.4", {"start": v(25, 61) * mm, "end": v(33.5, 61) * mm});
            skLineSegment(sketch, "E206.1.9.0", {"start": v(35, 65) * mm, "end": v(33.5, 64) * mm});
            skLineSegment(sketch, "E206.1.9.1", {"start": v(25, 64) * mm, "end": v(33.5, 64) * mm});
            skLineSegment(sketch, "E206.1.9.2", {"start": v(33.5, 66) * mm, "end": v(35, 65) * mm});
            skLineSegment(sketch, "E206.1.9.3", {"start": v(25, 64) * mm, "end": v(25, 66) * mm});
            skLineSegment(sketch, "E206.1.9.4", {"start": v(25, 66) * mm, "end": v(33.5, 66) * mm});
            skLineSegment(sketch, "E206.1.10.0", {"start": v(35, 70) * mm, "end": v(33.5, 69) * mm});
            skLineSegment(sketch, "E206.1.10.1", {"start": v(25, 69) * mm, "end": v(33.5, 69) * mm});
            skLineSegment(sketch, "E206.1.10.2", {"start": v(33.5, 71) * mm, "end": v(35, 70) * mm});
            skLineSegment(sketch, "E206.1.10.3", {"start": v(25, 69) * mm, "end": v(25, 71) * mm});
            skLineSegment(sketch, "E206.1.10.4", {"start": v(25, 71) * mm, "end": v(33.5, 71) * mm});
            skLineSegment(sketch, "E206.1.11.0", {"start": v(35, 75) * mm, "end": v(33.5, 74) * mm});
            skLineSegment(sketch, "E206.1.11.1", {"start": v(25, 74) * mm, "end": v(33.5, 74) * mm});
            skLineSegment(sketch, "E206.1.11.2", {"start": v(33.5, 76) * mm, "end": v(35, 75) * mm});
            skLineSegment(sketch, "E206.1.11.3", {"start": v(25, 74) * mm, "end": v(25, 76) * mm});
            skLineSegment(sketch, "E206.1.11.4", {"start": v(25, 76) * mm, "end": v(33.5, 76) * mm});
            skLineSegment(sketch, "E206.1.12.0", {"start": v(35, 80) * mm, "end": v(33.5, 79) * mm});
            skLineSegment(sketch, "E206.1.12.1", {"start": v(25, 79) * mm, "end": v(33.5, 79) * mm});
            skLineSegment(sketch, "E206.1.12.2", {"start": v(33.5, 81) * mm, "end": v(35, 80) * mm});
            skLineSegment(sketch, "E206.1.12.3", {"start": v(25, 79) * mm, "end": v(25, 81) * mm});
            skLineSegment(sketch, "E206.1.12.4", {"start": v(25, 81) * mm, "end": v(33.5, 81) * mm});
            skLineSegment(sketch, "E206.1.13.0", {"start": v(35, 85) * mm, "end": v(33.5, 84) * mm});
            skLineSegment(sketch, "E206.1.13.1", {"start": v(25, 84) * mm, "end": v(33.5, 84) * mm});
            skLineSegment(sketch, "E206.1.13.2", {"start": v(33.5, 86) * mm, "end": v(35, 85) * mm});
            skLineSegment(sketch, "E206.1.13.3", {"start": v(25, 84) * mm, "end": v(25, 86) * mm});
            skLineSegment(sketch, "E206.1.13.4", {"start": v(25, 86) * mm, "end": v(33.5, 86) * mm});
            skLineSegment(sketch, "E206.1.14.0", {"start": v(35, 90) * mm, "end": v(33.5, 89) * mm});
            skLineSegment(sketch, "E206.1.14.1", {"start": v(25, 89) * mm, "end": v(33.5, 89) * mm});
            skLineSegment(sketch, "E206.1.14.2", {"start": v(33.5, 91) * mm, "end": v(35, 90) * mm});
            skLineSegment(sketch, "E206.1.14.3", {"start": v(25, 89) * mm, "end": v(25, 91) * mm});
            skLineSegment(sketch, "E206.1.14.4", {"start": v(25, 91) * mm, "end": v(33.5, 91) * mm});
            skLineSegment(sketch, "E206.direction1", {"start": v(10, 19) * mm, "end": v(25, 19) * mm, "construction": true});
            skLineSegment(sketch, "E206.direction2", {"start": v(10, 19) * mm, "end": v(10, 24) * mm, "construction": true});
            skSolve(sketch);
        }
        {
            var Q0;
            Q0 = qSketchRegion(id + "F39", true);
            extrude(context, id + "F40", {"entities" : qUnion([Q0]), "operationType" : NewBodyOperationType.REMOVE, "endBound" : BoundingType.UP_TO_NEXT, "oppositeDirection" : true, "depth" : 25 * mm, "offsetDistance" : 25 * mm});
        }
        {
            var Q0;
            Q0=makeQuery(id+"F3.boolean.opBoolean","MERGE",FACE,{"derivedFrom":[makeQuery(id+"F1.opExtrude","SWEPT_FACE",FACE,{"disambiguationData":[OSD([sQuery(id+"F0.wireOp",EDGE,"E0.right")])]}),makeQuery(id+"F3.opExtrude","SWEPT_FACE",FACE,{"disambiguationData":[OSD([sQuery(id+"F2.wireOp",EDGE,"E30.0")])]})]});
            var sketch = newSketch(context, id + "F41", { "sketchPlane" : qUnion([Q0])});
            skLineSegment(sketch, "E207.bottom", {"start": v(-18.5, 72.64) * mm, "end": v(-10, 72.64) * mm});
            skLineSegment(sketch, "E207.top", {"start": v(-18.5, 70.64) * mm, "end": v(-10, 70.64) * mm});
            skLineSegment(sketch, "E207.right", {"start": v(-10, 72.64) * mm, "end": v(-10, 70.64) * mm});
            skLineSegment(sketch, "E208", {"start": v(-18.5, 70.64) * mm, "end": v(-20, 71.64) * mm});
            skLineSegment(sketch, "E209", {"start": v(-20, 71.64) * mm, "end": v(-18.5, 72.64) * mm});
            skLineSegment(sketch, "E210.0.1.0", {"start": v(-18.5, 75.64) * mm, "end": v(-10, 75.64) * mm});
            skLineSegment(sketch, "E210.0.1.1", {"start": v(-18.5, 77.64) * mm, "end": v(-10, 77.64) * mm});
            skLineSegment(sketch, "E210.0.1.2", {"start": v(-20, 76.64) * mm, "end": v(-18.5, 77.64) * mm});
            skLineSegment(sketch, "E210.0.1.3", {"start": v(-18.5, 75.64) * mm, "end": v(-20, 76.64) * mm});
            skLineSegment(sketch, "E210.0.1.4", {"start": v(-10, 77.64) * mm, "end": v(-10, 75.64) * mm});
            skLineSegment(sketch, "E210.0.2.0", {"start": v(-18.5, 80.64) * mm, "end": v(-10, 80.64) * mm});
            skLineSegment(sketch, "E210.0.2.1", {"start": v(-18.5, 82.64) * mm, "end": v(-10, 82.64) * mm});
            skLineSegment(sketch, "E210.0.2.2", {"start": v(-20, 81.64) * mm, "end": v(-18.5, 82.64) * mm});
            skLineSegment(sketch, "E210.0.2.3", {"start": v(-18.5, 80.64) * mm, "end": v(-20, 81.64) * mm});
            skLineSegment(sketch, "E210.0.2.4", {"start": v(-10, 82.64) * mm, "end": v(-10, 80.64) * mm});
            skLineSegment(sketch, "E210.0.3.0", {"start": v(-18.5, 85.64) * mm, "end": v(-10, 85.64) * mm});
            skLineSegment(sketch, "E210.0.3.1", {"start": v(-18.5, 87.64) * mm, "end": v(-10, 87.64) * mm});
            skLineSegment(sketch, "E210.0.3.2", {"start": v(-20, 86.64) * mm, "end": v(-18.5, 87.64) * mm});
            skLineSegment(sketch, "E210.0.3.3", {"start": v(-18.5, 85.64) * mm, "end": v(-20, 86.64) * mm});
            skLineSegment(sketch, "E210.0.3.4", {"start": v(-10, 87.64) * mm, "end": v(-10, 85.64) * mm});
            skLineSegment(sketch, "E210.0.4.0", {"start": v(-18.5, 90.64) * mm, "end": v(-10, 90.64) * mm});
            skLineSegment(sketch, "E210.0.4.1", {"start": v(-18.5, 92.64) * mm, "end": v(-10, 92.64) * mm});
            skLineSegment(sketch, "E210.0.4.2", {"start": v(-20, 91.64) * mm, "end": v(-18.5, 92.64) * mm});
            skLineSegment(sketch, "E210.0.4.3", {"start": v(-18.5, 90.64) * mm, "end": v(-20, 91.64) * mm});
            skLineSegment(sketch, "E210.0.4.4", {"start": v(-10, 92.64) * mm, "end": v(-10, 90.64) * mm});
            skLineSegment(sketch, "E210.1.0.0", {"start": v(-33.5, 70.64) * mm, "end": v(-25, 70.64) * mm});
            skLineSegment(sketch, "E210.1.0.1", {"start": v(-33.5, 72.64) * mm, "end": v(-25, 72.64) * mm});
            skLineSegment(sketch, "E210.1.0.2", {"start": v(-35, 71.64) * mm, "end": v(-33.5, 72.64) * mm});
            skLineSegment(sketch, "E210.1.0.3", {"start": v(-33.5, 70.64) * mm, "end": v(-35, 71.64) * mm});
            skLineSegment(sketch, "E210.1.0.4", {"start": v(-25, 72.64) * mm, "end": v(-25, 70.64) * mm});
            skLineSegment(sketch, "E210.1.1.0", {"start": v(-33.5, 75.64) * mm, "end": v(-25, 75.64) * mm});
            skLineSegment(sketch, "E210.1.1.1", {"start": v(-33.5, 77.64) * mm, "end": v(-25, 77.64) * mm});
            skLineSegment(sketch, "E210.1.1.2", {"start": v(-35, 76.64) * mm, "end": v(-33.5, 77.64) * mm});
            skLineSegment(sketch, "E210.1.1.3", {"start": v(-33.5, 75.64) * mm, "end": v(-35, 76.64) * mm});
            skLineSegment(sketch, "E210.1.1.4", {"start": v(-25, 77.64) * mm, "end": v(-25, 75.64) * mm});
            skLineSegment(sketch, "E210.1.2.0", {"start": v(-33.5, 80.64) * mm, "end": v(-25, 80.64) * mm});
            skLineSegment(sketch, "E210.1.2.1", {"start": v(-33.5, 82.64) * mm, "end": v(-25, 82.64) * mm});
            skLineSegment(sketch, "E210.1.2.2", {"start": v(-35, 81.64) * mm, "end": v(-33.5, 82.64) * mm});
            skLineSegment(sketch, "E210.1.2.3", {"start": v(-33.5, 80.64) * mm, "end": v(-35, 81.64) * mm});
            skLineSegment(sketch, "E210.1.2.4", {"start": v(-25, 82.64) * mm, "end": v(-25, 80.64) * mm});
            skLineSegment(sketch, "E210.1.3.0", {"start": v(-33.5, 85.64) * mm, "end": v(-25, 85.64) * mm});
            skLineSegment(sketch, "E210.1.3.1", {"start": v(-33.5, 87.64) * mm, "end": v(-25, 87.64) * mm});
            skLineSegment(sketch, "E210.1.3.2", {"start": v(-35, 86.64) * mm, "end": v(-33.5, 87.64) * mm});
            skLineSegment(sketch, "E210.1.3.3", {"start": v(-33.5, 85.64) * mm, "end": v(-35, 86.64) * mm});
            skLineSegment(sketch, "E210.1.3.4", {"start": v(-25, 87.64) * mm, "end": v(-25, 85.64) * mm});
            skLineSegment(sketch, "E210.1.4.0", {"start": v(-33.5, 90.64) * mm, "end": v(-25, 90.64) * mm});
            skLineSegment(sketch, "E210.1.4.1", {"start": v(-33.5, 92.64) * mm, "end": v(-25, 92.64) * mm});
            skLineSegment(sketch, "E210.1.4.2", {"start": v(-35, 91.64) * mm, "end": v(-33.5, 92.64) * mm});
            skLineSegment(sketch, "E210.1.4.3", {"start": v(-33.5, 90.64) * mm, "end": v(-35, 91.64) * mm});
            skLineSegment(sketch, "E210.1.4.4", {"start": v(-25, 92.64) * mm, "end": v(-25, 90.64) * mm});
            skLineSegment(sketch, "E210.direction1", {"start": v(-20, 71.64) * mm, "end": v(-35, 71.64) * mm, "construction": true});
            skLineSegment(sketch, "E210.direction2", {"start": v(-20, 71.64) * mm, "end": v(-20, 76.64) * mm, "construction": true});
            skSolve(sketch);
        }
        {
            var Q0;
            Q0 = qSketchRegion(id + "F41", true);
            extrude(context, id + "F42", {"entities" : qUnion([Q0]), "operationType" : NewBodyOperationType.REMOVE, "endBound" : BoundingType.UP_TO_NEXT, "oppositeDirection" : true, "depth" : 25 * mm, "offsetDistance" : 25 * mm});
        }
        {
            var Q0;
            Q0=makeQuery(id+"F38.boolean.opBoolean","MERGE",FACE,{"derivedFrom":[makeQuery(id+"F3.opExtrude","CAP_FACE",FACE,{"disambiguationData":[OSD([sQuery(id+"F2.wireOp",EDGE,"E5.bottom"),sQuery(id+"F2.wireOp",EDGE,"E5.top"),sQuery(id+"F2.wireOp",EDGE,"E5.left"),sQuery(id+"F2.wireOp",EDGE,"E5.right"),sQuery(id+"F2.wireOp",EDGE,"E10"),sQuery(id+"F2.wireOp",EDGE,"E12"),sQuery(id+"F2.wireOp",EDGE,"E21"),sQuery(id+"F2.wireOp",EDGE,"E22"),sQuery(id+"F2.wireOp",EDGE,"E23"),sQuery(id+"F2.wireOp",EDGE,"E24.filletArc"),sQuery(id+"F2.wireOp",EDGE,"E25.trimOffspring"),sQuery(id+"F2.wireOp",EDGE,"E30.0"),sQuery(id+"F2.wireOp",EDGE,"E16.0"),sQuery(id+"F2.wireOp",EDGE,"E33.0.2"),sQuery(id+"F2.wireOp",EDGE,"E29.0"),sQuery(id+"F2.wireOp",EDGE,"E33.0.4"),sQuery(id+"F2.wireOp",EDGE,"E32.0"),sQuery(id+"F2.wireOp",EDGE,"E33.0.6"),sQuery(id+"F2.wireOp",EDGE,"E33.0.7"),sQuery(id+"F2.wireOp",EDGE,"E34.0"),sQuery(id+"F2.wireOp",EDGE,"E34.1"),sQuery(id+"F2.wireOp",EDGE,"E34.3"),sQuery(id+"F2.wireOp",EDGE,"E34.4"),sQuery(id+"F2.wireOp",EDGE,"E35.filletArc"),sQuery(id+"F2.wireOp",EDGE,"E36.filletArc"),sQuery(id+"F2.wireOp",EDGE,"E37"),sQuery(id+"F2.wireOp",EDGE,"E38"),sQuery(id+"F2.wireOp",EDGE,"E39")])],"isStart":false}),makeQuery(id+"F38.opExtrude","CAP_FACE",FACE,{"disambiguationData":[OSD([sQuery(id+"F37.wireOp",EDGE,"E192.0"),sQuery(id+"F37.wireOp",EDGE,"E194"),sQuery(id+"F37.wireOp",EDGE,"E195"),sQuery(id+"F37.wireOp",EDGE,"E196"),sQuery(id+"F37.wireOp",EDGE,"E191.0"),sQuery(id+"F37.wireOp",EDGE,"E198.trimOffspring")])],"isStart":true})]});
            var sketch = newSketch(context, id + "F43", { "sketchPlane" : qUnion([Q0])});
            skPoint(sketch, "E211.0", {"position": v(6, 104) * mm});
            skPoint(sketch, "E212.0", {"position": v(154, 104) * mm});
            skPoint(sketch, "E213.0", {"position": v(154, 6) * mm});
            skPoint(sketch, "E214.0", {"position": v(6, 6) * mm});
            skCircle(sketch, "E215", {"center": v(6, 104) * mm, "radius": 1.1 * mm});
            skCircle(sketch, "E216", {"center": v(66, 104) * mm, "radius": 1.1 * mm});
            skCircle(sketch, "E217", {"center": v(154, 104) * mm, "radius": 1.1 * mm});
            skCircle(sketch, "E218", {"center": v(154, 6) * mm, "radius": 1.1 * mm});
            skCircle(sketch, "E219", {"center": v(6, 6) * mm, "radius": 1.1 * mm});
            skSolve(sketch);
        }
        {
            var Q0;
            Q0 = qSketchRegion(id + "F43", true);
            extrude(context, id + "F44", {"entities" : qUnion([Q0]), "operationType" : NewBodyOperationType.REMOVE, "oppositeDirection" : true, "depth" : 10 * mm, "offsetDistance" : 25 * mm});
        }
        {
            var Q0;
            Q0=makeQuery(id+"F38.boolean.opBoolean","MERGE",FACE,{"derivedFrom":[makeQuery(id+"F3.opExtrude","CAP_FACE",FACE,{"disambiguationData":[OSD([sQuery(id+"F2.wireOp",EDGE,"E5.bottom"),sQuery(id+"F2.wireOp",EDGE,"E5.top"),sQuery(id+"F2.wireOp",EDGE,"E5.left"),sQuery(id+"F2.wireOp",EDGE,"E5.right"),sQuery(id+"F2.wireOp",EDGE,"E10"),sQuery(id+"F2.wireOp",EDGE,"E12"),sQuery(id+"F2.wireOp",EDGE,"E21"),sQuery(id+"F2.wireOp",EDGE,"E22"),sQuery(id+"F2.wireOp",EDGE,"E23"),sQuery(id+"F2.wireOp",EDGE,"E24.filletArc"),sQuery(id+"F2.wireOp",EDGE,"E25.trimOffspring"),sQuery(id+"F2.wireOp",EDGE,"E30.0"),sQuery(id+"F2.wireOp",EDGE,"E16.0"),sQuery(id+"F2.wireOp",EDGE,"E33.0.2"),sQuery(id+"F2.wireOp",EDGE,"E29.0"),sQuery(id+"F2.wireOp",EDGE,"E33.0.4"),sQuery(id+"F2.wireOp",EDGE,"E32.0"),sQuery(id+"F2.wireOp",EDGE,"E33.0.6"),sQuery(id+"F2.wireOp",EDGE,"E33.0.7"),sQuery(id+"F2.wireOp",EDGE,"E34.0"),sQuery(id+"F2.wireOp",EDGE,"E34.1"),sQuery(id+"F2.wireOp",EDGE,"E34.3"),sQuery(id+"F2.wireOp",EDGE,"E34.4"),sQuery(id+"F2.wireOp",EDGE,"E35.filletArc"),sQuery(id+"F2.wireOp",EDGE,"E36.filletArc"),sQuery(id+"F2.wireOp",EDGE,"E37"),sQuery(id+"F2.wireOp",EDGE,"E38"),sQuery(id+"F2.wireOp",EDGE,"E39")])],"isStart":false}),makeQuery(id+"F38.opExtrude","CAP_FACE",FACE,{"disambiguationData":[OSD([sQuery(id+"F37.wireOp",EDGE,"E192.0"),sQuery(id+"F37.wireOp",EDGE,"E194"),sQuery(id+"F37.wireOp",EDGE,"E195"),sQuery(id+"F37.wireOp",EDGE,"E196"),sQuery(id+"F37.wireOp",EDGE,"E191.0"),sQuery(id+"F37.wireOp",EDGE,"E198.trimOffspring")])],"isStart":true})]});
            var sketch = newSketch(context, id + "F45", { "sketchPlane" : qUnion([Q0])});
            skLineSegment(sketch, "E220.0", {"start": v(6, 110) * mm, "end": v(154, 110) * mm});
            skArc(sketch, "E221.0", {"start": v(6, 110) * mm, "mid": v(1.76, 108.24) * mm, "end": v(0, 104) * mm});
            skLineSegment(sketch, "E222.0", {"start": v(0, 6) * mm, "end": v(0, 104) * mm});
            skArc(sketch, "E223.0", {"start": v(0, 6) * mm, "mid": v(1.76, 1.76) * mm, "end": v(6, 0) * mm});
            skLineSegment(sketch, "E224.0", {"start": v(6, 0) * mm, "end": v(154, 0) * mm});
            skArc(sketch, "E225.0", {"start": v(154, 0) * mm, "mid": v(158.24, 1.76) * mm, "end": v(160, 6) * mm});
            skLineSegment(sketch, "E226.0", {"start": v(160, 6) * mm, "end": v(160, 104) * mm});
            skArc(sketch, "E227.0", {"start": v(160, 104) * mm, "mid": v(158.24, 108.24) * mm, "end": v(154, 110) * mm});
            skCircle(sketch, "E228", {"center": v(6, 104) * mm, "radius": 1.6 * mm});
            skCircle(sketch, "E229", {"center": v(154, 104) * mm, "radius": 1.6 * mm});
            skCircle(sketch, "E230", {"center": v(154, 6) * mm, "radius": 1.6 * mm});
            skCircle(sketch, "E231", {"center": v(6, 6) * mm, "radius": 1.6 * mm});
            skCircle(sketch, "E232.0", {"center": v(66, 104) * mm, "radius": 1.6 * mm});
            skSolve(sketch);
        }
        {
            var Q0;
            Q0 = qSketchRegion(id + "F45", true);
            extrude(context, id + "F46", {"entities" : qUnion([Q0]), "depth" : 2 * mm, "offsetDistance" : 25 * mm});
        }
        {
            var Q0;
            Q0=makeQuery(id+"F46.opExtrude","CAP_FACE",FACE,{"disambiguationData":[OSD([sQuery(id+"F45.wireOp",EDGE,"E220.0"),sQuery(id+"F45.wireOp",EDGE,"E221.0"),sQuery(id+"F45.wireOp",EDGE,"E222.0"),sQuery(id+"F45.wireOp",EDGE,"E223.0"),sQuery(id+"F45.wireOp",EDGE,"E224.0"),sQuery(id+"F45.wireOp",EDGE,"E225.0"),sQuery(id+"F45.wireOp",EDGE,"E226.0"),sQuery(id+"F45.wireOp",EDGE,"E227.0"),sQuery(id+"F45.wireOp",EDGE,"E228"),sQuery(id+"F45.wireOp",EDGE,"E229"),sQuery(id+"F45.wireOp",EDGE,"E230"),sQuery(id+"F45.wireOp",EDGE,"E231"),sQuery(id+"F45.wireOp",EDGE,"E232.0")])],"isStart":true});
            var sketch = newSketch(context, id + "F47", { "sketchPlane" : qUnion([Q0])});
            skLineSegment(sketch, "E233.0", {"start": v(-148, 108) * mm, "end": v(-73, 108) * mm});
            skPoint(sketch, "E234.0", {"position": v(-73, 109) * mm});
            skLineSegment(sketch, "E235.0", {"start": v(-150, 110) * mm, "end": v(-71, 110) * mm});
            skPoint(sketch, "E236.0", {"position": v(-148, 109) * mm});
            skLineSegment(sketch, "E237.0", {"start": v(-158, 10) * mm, "end": v(-158, 95) * mm});
            skLineSegment(sketch, "E238.0", {"start": v(-10, 2) * mm, "end": v(-150, 2) * mm});
            skPoint(sketch, "E239.0", {"position": v(-2, 56) * mm});
            skLineSegment(sketch, "E240.0", {"start": v(-56, 108) * mm, "end": v(-15, 108) * mm});
            skLineSegment(sketch, "E241.0", {"start": v(-160, 6) * mm, "end": v(-160, 104) * mm});
            skLineSegment(sketch, "E242.0", {"start": v(-6, 0) * mm, "end": v(-154, 0) * mm});
            skLineSegment(sketch, "E243.0", {"start": v(0, 6) * mm, "end": v(0, 104) * mm});
            skLineSegment(sketch, "E244.0", {"start": v(-6, 110) * mm, "end": v(-154, 110) * mm});
            skLineSegment(sketch, "E245", {"start": v(-15, 108) * mm, "end": v(-15, 106) * mm});
            skLineSegment(sketch, "E246", {"start": v(-15, 106) * mm, "end": v(-56, 106) * mm});
            skLineSegment(sketch, "E247", {"start": v(-56, 106) * mm, "end": v(-56, 108) * mm});
            skLineSegment(sketch, "E248", {"start": v(-150, 2) * mm, "end": v(-150, 4) * mm});
            skLineSegment(sketch, "E249", {"start": v(-150, 4) * mm, "end": v(-10, 4) * mm});
            skLineSegment(sketch, "E250", {"start": v(-10, 4) * mm, "end": v(-10, 2) * mm});
            skLineSegment(sketch, "E251", {"start": v(-158, 95) * mm, "end": v(-156, 95) * mm});
            skLineSegment(sketch, "E252", {"start": v(-156, 95) * mm, "end": v(-156, 10) * mm});
            skLineSegment(sketch, "E253", {"start": v(-156, 10) * mm, "end": v(-158, 10) * mm});
            skLineSegment(sketch, "E254.0", {"start": v(-2, 95) * mm, "end": v(-2, 10) * mm});
            skLineSegment(sketch, "E255", {"start": v(-2, 95) * mm, "end": v(-4, 95) * mm});
            skLineSegment(sketch, "E256", {"start": v(-4, 95) * mm, "end": v(-4, 10) * mm});
            skLineSegment(sketch, "E257", {"start": v(-4, 10) * mm, "end": v(-2, 10) * mm});
            skLineSegment(sketch, "E258", {"start": v(-148, 108) * mm, "end": v(-148, 110) * mm});
            skLineSegment(sketch, "E259", {"start": v(-73, 108) * mm, "end": v(-73, 110) * mm});
            skSolve(sketch);
        }
        {
            var Q0;
            Q0 = qSketchRegion(id + "F47", true);
            extrude(context, id + "F48", {"entities" : qUnion([Q0]), "operationType" : NewBodyOperationType.ADD, "depth" : 2 * mm, "offsetDistance" : 25 * mm});
        }
    });
